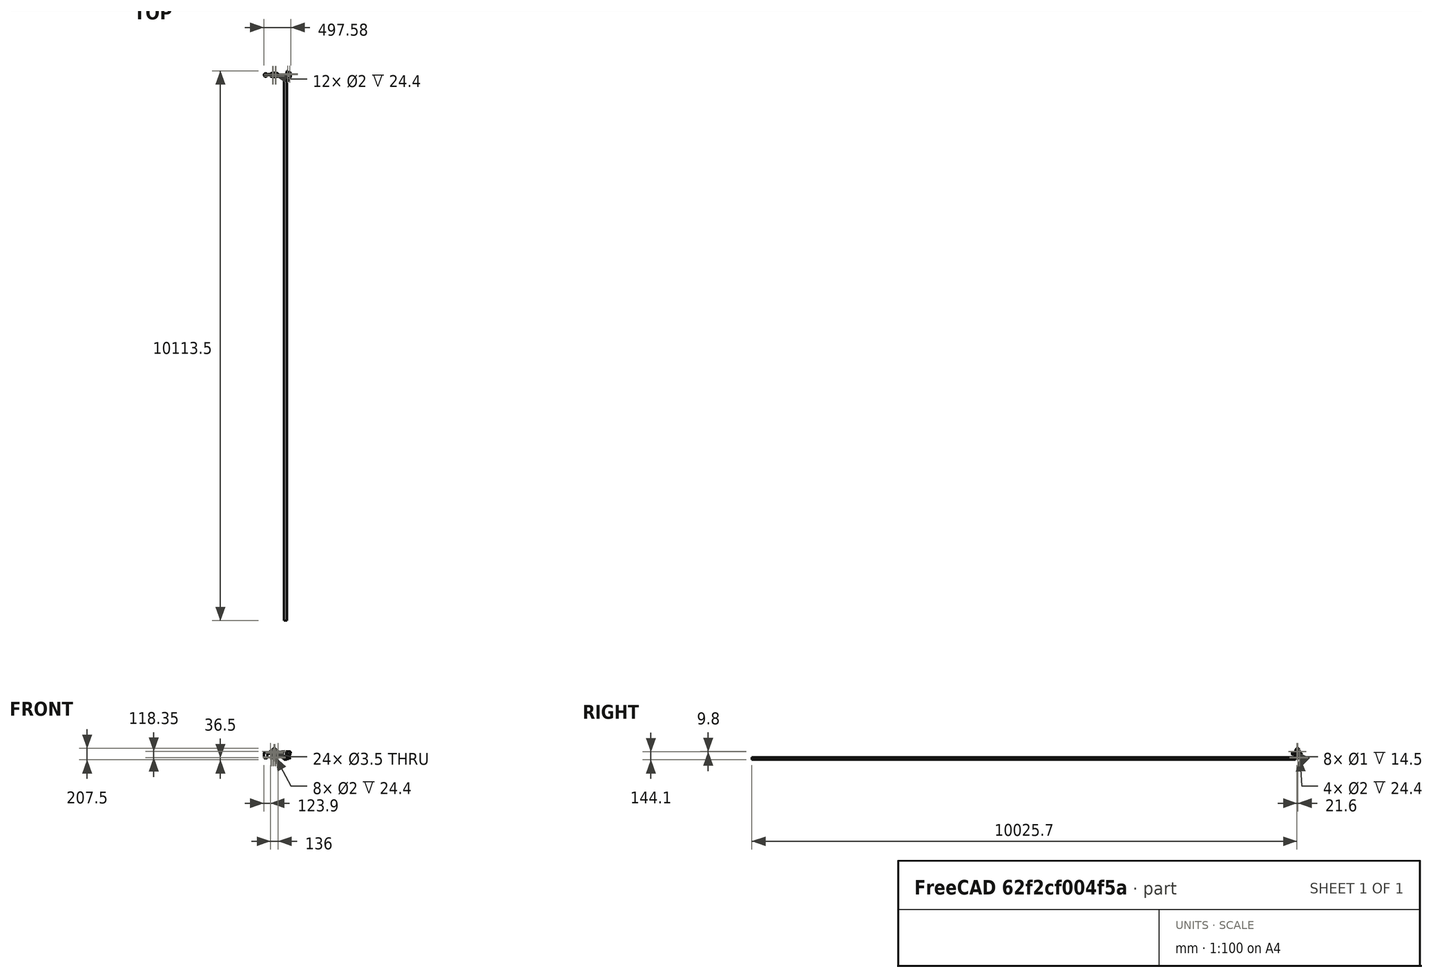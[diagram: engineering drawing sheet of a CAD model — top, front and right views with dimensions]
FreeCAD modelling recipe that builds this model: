
FCSTD DOCUMENT  (FreeCAD 0.16R6710 (Git))
Label: head_zowi_makerbot
License: CC-BY 3.0
LicenseURL: http://creativecommons.org/licenses/by/3.0/
objects: Part::Feature×140, Part::Cut×55, Part::Cylinder×55, Part::Box×45, Part::MultiFuse×37, Sketcher::SketchObject×19, Part::FeaturePython×17, App::DocumentObjectGroup×10, PartDesign::Pocket×10, Part::Mirroring×9, Part::Fillet×9, PartDesign::Pad×9, Part::Chamfer×6, Part::Prism×3, PartDesign::Fillet×2, Part::MultiCommon×2, Mesh::Feature×1
note: 437 computed .brp shape members not serialized (recipe doc carries the construction recipe); baked Part::Feature solids carry a one-line shape summary decoded from their .brp

FEATURE [Part::Feature] Part__Feature013  label="Servo-D1"
  Placement = pos=(26.5,9.5,100.6) rot=(0,1,0;3.14159rad)
  shape: bbox 55.5 x 20 x 41.74 mm, 365 faces (baked)
FEATURE [Part::Feature] Part__Feature014  label="Servo-D2"
  Placement = pos=(0,0,13) rot=(0.57735,0.57735,0.57735;2.0944rad)
  shape: bbox 41.74 x 55.5 x 20 mm, 365 faces (baked)
FEATURE [Part::Feature] Part__Feature008  label="J1"
  Placement = pos=(-10.8,44.37,77.54) rot=(0.707107,0.707107,0;3.14159rad)
  shape: bbox 11.7 x 15.49 x 2.5 mm, 224 faces (baked)
FEATURE [Part::Feature] Part__Feature009  label="J2"
  Placement = pos=(-10.8,62.15,77.54) rot=(0.707107,0.707107,0;3.14159rad)
  shape: bbox 11.7 x 15.49 x 2.5 mm, 224 faces (baked)
FEATURE [Part::Feature] Part__Feature007  label="J4"
  Placement = pos=(-10.8,59.6199,125.78) rot=(0,0,-1;1.5708rad)
  shape: bbox 11.65 x 20.57 x 2.5 mm, 290 faces (baked)
FEATURE [Part::Feature] Part__Feature010  label="J16"
  Placement = pos=(-9.55,7.19908,100.417) rot=(0.57735,0.57735,-0.57735;2.0944rad)
  shape: bbox 2.94 x 5.43 x 7.98 mm, 414 faces, 0 solids (baked)
FEATURE [Part::Feature] Part__Feature005  label="PCB"
  Placement = pos=(-12.3914,5,75) rot=(0.57735,0.57735,0.57735;2.0944rad)
  shape: bbox 1.591 x 68.6 x 53.36 mm, 426 faces (baked)
FEATURE [Part::Feature] Part__Feature004  label="J010"
  Placement = pos=(-10.8,14.8841,83.3059) rot=(0.707107,0.707107,0;3.14159rad)
  shape: bbox 10.92 x 14.61 x 8.89 mm, 41 faces (baked)
FEATURE [Part::Feature] Part__Feature011  label="U1"
  Placement = pos=(-9.2,12.159,115.511) rot=(0.57735,-0.57735,-0.57735;2.0944rad)
  shape: bbox 2.435 x 26.9 x 13 mm, 503 faces (baked)
FEATURE [Part::Feature] Part__Feature006  label="J8"
  Placement = pos=(-10.8,37.7759,125.78) rot=(0,0,-1;1.5708rad)
  shape: bbox 11.65 x 20.57 x 2.5 mm, 290 faces (baked)
FEATURE [App::DocumentObjectGroup] Group001  label="placa"
  Group = -> [Part__Feature008,Part__Feature009,Part__Feature007,Part__Feature010,Part__Feature005,Part__Feature004,Part__Feature011,Part__Feature006]
FEATURE [Part::Box] Box  label="Cube"
  Height = 24
  Length = 72
  Placement = pos=(-15,-29,-3) rot=(0,0,1;0rad)
  Width = 58
FEATURE [Part::Box] Box001  label="Cube001"
  Height = 25
  Length = 47
  Placement = pos=(-1,-21,2) rot=(0,0,1;0rad)
  Width = 42
FEATURE [Part::Box] Box002  label="Cube002"
  Height = 38
  Length = 28
  Placement = pos=(37,-45,1) rot=(0,0,1;0rad)
  Width = 88
FEATURE [Part::Box] Box003  label="Cube003"
  Height = 38
  Length = 28
  Placement = pos=(-33,-45,1) rot=(0,0,1;0rad)
  Width = 88
FEATURE [Part::Cut] Cut
  Base = -> Box
  Tool = -> Box001
FEATURE [Part::Cut] Cut001
  Base = -> Cut
  Tool = -> Box002
FEATURE [Part::Cut] Cut002
  Base = -> Cut001
  Tool = -> Box003
FEATURE [Part::Box] Box004  label="Cube004"
  Height = 60
  Length = 44
  Placement = pos=(-5,-24,-5) rot=(0,0,1;0rad)
  Width = 61
FEATURE [Part::Mirroring] Part__Mirroring  label="Servo-D1 (Mirror #1)"
  Base = (0,0,0)
  Normal = (0,1,0)
  Placement = pos=(0,72,0) rot=(0,0,1;0rad)
  Source = -> Part__Feature013
FEATURE [Part::Mirroring] Part__Mirroring001  label="Servo-D2 (Mirror #2)"
  Base = (0,0,0)
  Normal = (0,1,0)
  Placement = pos=(0,72,0) rot=(0,0,1;0rad)
  Source = -> Part__Feature014
FEATURE [Part::Cylinder] Cylinder003  label="Joint-D005"
  Angle = 360
  Height = 74.5
  Placement = pos=(-22,9.5,12) rot=(0,1,0;1.5708rad)
  Radius = 1.75
FEATURE [Part::Fillet] Fillet
  Base = -> Cut002
  Edges = 4 edges r=10: [Edge1,Edge3,Edge5,Edge14]
FEATURE [Part::Cylinder] Cylinder002  label="Joint-D004"
  Angle = 360
  Height = 53
  Placement = pos=(-9,9.5,12) rot=(0,1,0;1.5708rad)
  Radius = 10.5
FEATURE [Part::MultiFuse] Fusion
  Shapes = -> [Cylinder002]
FEATURE [Part::Cylinder] Cylinder004  label="Joint-D006"
  Angle = 360
  Height = 74.5
  Placement = pos=(16,9.5,12) rot=(0,1,0;1.5708rad)
  Radius = 5.5
FEATURE [Part::Cut] Cut003
  Base = -> Fusion
  Tool = -> Box004
FEATURE [Part::Cylinder] Cylinder005  label="Joint-D007"
  Angle = 360
  Height = 74.5
  Placement = pos=(-51,9.5,12) rot=(0,1,0;1.5708rad)
  Radius = 1.75
FEATURE [Part::Cut] Cut004
  Base = -> Cut003
  Tool = -> Cylinder004
FEATURE [Part::Cut] Cut005
  Base = -> Cut004
  Tool = -> Cylinder005
FEATURE [Part::Cylinder] Cylinder006  label="Joint-D008"
  Angle = 360
  Height = 74.5
  Placement = pos=(41.8,9.5,12) rot=(0,1,0;1.5708rad)
  Radius = 11
FEATURE [Part::Cut] Cut006
  Base = -> Cut005
  Tool = -> Cylinder006
FEATURE [Part::Cylinder] Cylinder007  label="Joint-D009"
  Angle = 360
  Height = 23.5
  Placement = pos=(16.8,9.5,58.3) rot=(0,1,0;3.14159rad)
  Radius = 11
FEATURE [Part::Cylinder] Cylinder008  label="Joint-D010"
  Angle = 360
  Height = 21.5
  Placement = pos=(16,-24.5,7) rot=(0,1,0;1.5708rad)
  Radius = 1.75
FEATURE [Part::Cylinder] Cylinder009  label="Joint-D011"
  Angle = 360
  Height = 21.5
  Placement = pos=(32,-24.5,7) rot=(0,1,0;1.5708rad)
  Radius = 3
FEATURE [Part::MultiFuse] Fusion001
  Shapes = -> [Cylinder009,Cylinder008]
FEATURE [Part::MultiFuse] Fusion002
  Placement = pos=(0,0,10) rot=(0,0,1;0rad)
  Shapes = -> [Cylinder009,Cylinder008]
FEATURE [Part::MultiFuse] Fusion003
  Placement = pos=(0,49,0) rot=(0,0,1;0rad)
  Shapes = -> [Cylinder009,Cylinder008]
FEATURE [Part::MultiFuse] Fusion004
  Placement = pos=(0,49,10) rot=(0,0,1;0rad)
  Shapes = -> [Cylinder009,Cylinder008]
FEATURE [Part::Box] Box006  label="Cube006"
  Height = 21
  Length = 4
  Placement = pos=(25.5,-28,2) rot=(0,0,1;0rad)
  Width = 56
FEATURE [Part::Cylinder] Cylinder010  label="Joint-D012"
  Angle = 360
  Height = 74.5
  Placement = pos=(17,9.5,12) rot=(0,0,1;0rad)
  Radius = 5.5
FEATURE [Part::Box] Box007  label="Cube007"
  Height = 6
  Length = 3
  Placement = pos=(18.5,-28,4) rot=(0,0,1;0rad)
  Width = 56
FEATURE [Part::Box] Box008  label="Cube008"
  Height = 6
  Length = 3
  Placement = pos=(18.5,-28,14) rot=(0,0,1;0rad)
  Width = 56
FEATURE [Part::Cylinder] Cylinder011  label="Joint-D013"
  Angle = 360
  Height = 74.5
  Placement = pos=(-3,9.5,12) rot=(0,1,0;1.5708rad)
  Radius = 2.75
FEATURE [Part::Box] Box009  label="Cube009"
  Height = 5
  Length = 80
  Placement = pos=(-23,-4,63) rot=(0,0,1;0rad)
  Width = 80
FEATURE [Part::Box] Box010  label="Cube010"
  Height = 9
  Length = 7
  Placement = pos=(-1,-1,63) rot=(0,0,1;0rad)
  Width = 74
FEATURE [Part::Box] Box011  label="Cube011"
  Height = 9
  Length = 7
  Placement = pos=(47,-1,63) rot=(0,0,1;0rad)
  Width = 74
FEATURE [Part::MultiFuse] Fusion005
  Placement = pos=(44,39,98) rot=(0,1,0;1.5708rad)
  Shapes = -> [Cylinder009,Cylinder008]
FEATURE [Part::MultiFuse] Fusion008
  Placement = pos=(44,29,98) rot=(0,1,0;1.5708rad)
  Shapes = -> [Cylinder009,Cylinder008]
FEATURE [Part::MultiFuse] Fusion009
  Placement = pos=(-5,39,98) rot=(0,1,0;1.5708rad)
  Shapes = -> [Cylinder009,Cylinder008]
FEATURE [Part::MultiFuse] Fusion010
  Placement = pos=(-5,29,98) rot=(0,1,0;1.5708rad)
  Shapes = -> [Cylinder009,Cylinder008]
FEATURE [Part::Box] Box012  label="Cube012"
  Height = 9
  Length = 70
  Placement = pos=(-6,8.5,70) rot=(0,0,1;0rad)
  Width = 2
FEATURE [Part::MultiFuse] Fusion011
  Shapes = -> [Box012,Fusion009,Fusion010,Fusion008,Fusion005]
FEATURE [Part::MultiFuse] Fusion012
  Placement = pos=(0,53,0) rot=(0,0,1;0rad)
  Shapes = -> [Box012,Fusion009,Fusion010,Fusion008,Fusion005]
FEATURE [Part::MultiFuse] Fusion013
  Shapes = -> [Box009,Box011,Box010]
FEATURE [Part::Cut] Cut018
  Base = -> Fusion013
  Tool = -> Fusion012
FEATURE [Part::Cut] Cut019
  Base = -> Cut018
  Tool = -> Fusion011
FEATURE [Part::Box] Box014  label="Cube014"
  Height = 43
  Length = 41
  Placement = pos=(6,-1,59) rot=(0,0,1;0rad)
  Width = 21
FEATURE [Part::Box] Box015  label="Cube015"
  Height = 43
  Length = 41
  Placement = pos=(6,52,59) rot=(0,0,1;0rad)
  Width = 21
FEATURE [Part::Cut] Cut020
  Base = -> Cut019
  Tool = -> Box014
FEATURE [Part::Cut] Cut021
  Base = -> Cut020
  Tool = -> Box015
FEATURE [Part::Box] Box016  label="Cube016"
  Height = 12
  Length = 6
  Placement = pos=(-11.5,3,69) rot=(0,0,1;0rad)
  Width = 3
FEATURE [Part::Box] Box017  label="Cube017"
  Height = 12
  Length = 16
  Placement = pos=(-20,-1,63) rot=(0,0,1;0rad)
  Width = 74
FEATURE [Part::Box] Box018  label="Cube018"
  Height = 12
  Length = 6
  Placement = pos=(-11.5,66,69) rot=(0,0,1;0rad)
  Width = 3
FEATURE [Part::MultiFuse] Fusion014
  Shapes = -> [Cut021,Box017]
FEATURE [Part::Cut] Cut022
  Base = -> Fusion014
  Tool = -> Box016
FEATURE [Part::Cut] Cut023
  Base = -> Cut022
  Tool = -> Box018
FEATURE [PartDesign::Fillet] Fillet011  label="horn"
  Placement = pos=(38.5,9.5,13) rot=(0,0,-1;1.5708rad)
  Radius = 0.5
FEATURE [Part::Cylinder] Cylinder021  label="Joint-D014"
  Angle = 360
  Height = 52.5
  Placement = pos=(19,9.5,20.35) rot=(0,1,0;1.5708rad)
  Radius = 1
FEATURE [Part::Cylinder] Cylinder022  label="Joint-D015"
  Angle = 360
  Height = 52.5
  Placement = pos=(19,2,9.5) rot=(0,1,0;1.5708rad)
  Radius = 1
FEATURE [Part::Cylinder] Cylinder023  label="Joint-D016"
  Angle = 360
  Height = 52.5
  Placement = pos=(19,17,9.5) rot=(0,1,0;1.5708rad)
  Radius = 1
FEATURE [Part::MultiFuse] Fusion017
  Placement = pos=(0,0,-1) rot=(0,0,1;0rad)
  Shapes = -> [Cylinder022,Cylinder021,Cylinder023]
FEATURE [Part::MultiFuse] Fusion018
  Placement = pos=(4,0,101) rot=(0,1,0;1.5708rad)
  Shapes = -> [Cylinder022,Cylinder021,Cylinder023]
FEATURE [PartDesign::Fillet] Fillet012  label="horn001"
  Placement = pos=(16.8,9.5,62.5) rot=(-0.57735,0.57735,-0.57735;2.0944rad)
  Radius = 0.5
FEATURE [Part::Mirroring] Part__Mirroring003  label="horn (Mirror #4)"
  Base = (41.6,1.90735e-06,13)
  Normal = (0,1,-1.19209e-07)
  Placement = pos=(0,72,0) rot=(0,0,1;0rad)
  Source = -> Fillet011
FEATURE [Part::Mirroring] Part__Mirroring004  label="horn001 (Mirror #5)"
  Base = (16.8,7.62939e-06,59.3998)
  Normal = (0,1,-1.19209e-07)
  Placement = pos=(0,72,0) rot=(0,0,1;0rad)
  Source = -> Fillet012
FEATURE [Part::Chamfer] Chamfer
  Base = -> Fillet
  Edges = 3 edges r=3: [Edge18,Edge33,Edge37]
FEATURE [Part::Cut] Cut008
  Base = -> Chamfer
  Tool = -> Cylinder003
FEATURE [Part::Cut] Cut010
  Base = -> Cut008
  Tool = -> Box006
FEATURE [Part::Cut] Cut011
  Base = -> Cut010
  Tool = -> Box008
FEATURE [Part::Cut] Cut012
  Base = -> Cut011
  Tool = -> Box007
FEATURE [Part::Cut] Cut013
  Base = -> Cut012
  Tool = -> Fusion004
FEATURE [Part::Cut] Cut014
  Base = -> Cut013
  Tool = -> Fusion003
FEATURE [Part::Cut] Cut015
  Base = -> Cut014
  Tool = -> Fusion002
FEATURE [Part::Cut] Cut016
  Base = -> Cut015
  Tool = -> Fusion001
FEATURE [Part::Cut] Cut017  label="pie"
  Base = -> Cut016
  Tool = -> Cylinder011
FEATURE [Part::Box] Box024  label="Cube024"
  Height = 23
  Length = 6
  Placement = pos=(0,19,7) rot=(0,0,1;0rad)
  Width = 36
FEATURE [Part::Cut] Cut039  label="pie-D"
  Base = -> Cut017
  Placement = pos=(0,0,1) rot=(0,0,1;0rad)
  Tool = -> Box024
FEATURE [Part::Mirroring] Part__Mirroring006  label="pie-I"
  Base = (0,0,0)
  Normal = (0,1,0)
  Placement = pos=(0,72,0) rot=(0,0,1;0rad)
  Source = -> Cut039
FEATURE [Part::Cut] Cut044
  Base = -> Cut006
  Tool = -> Box004
FEATURE [Part::Cut] Cut045
  Base = -> Cut044
  Tool = -> Cylinder007
FEATURE [Part::Cut] Cut046
  Base = -> Cut045
  Tool = -> Fusion018
FEATURE [Part::Cut] Cut047
  Base = -> Cut046
  Tool = -> Fusion017
FEATURE [Part::Cut] Cut048
  Base = -> Cut047
  Placement = pos=(0,0,1) rot=(0,0,1;0rad)
  Tool = -> Cylinder010
FEATURE [Part::Chamfer] Chamfer001
  Base = -> Cut048
  Edges = 1 edges r=4: [Edge61]
FEATURE [Part::Chamfer] Chamfer002  label="pata-D"
  Base = -> Chamfer001
  Edges = 1 edges r=8: [Edge58]
FEATURE [Part::Mirroring] Part__Mirroring007  label="pata-I"
  Base = (17.5,3.8147e-06,32.25)
  Normal = (0,1,-1.19209e-07)
  Placement = pos=(0,72,0) rot=(0,0,1;0rad)
  Source = -> Chamfer002
FEATURE [Part::Cylinder] Cylinder012  label="Cylinder030"
  Angle = 360
  Height = 31
  Placement = pos=(-8.5,92,71.5) rot=(1,0,0;1.5708rad)
  Radius = 1.75
FEATURE [Part::Cut] Cut024
  Base = -> Cut023
  Tool = -> Cylinder012
FEATURE [Part::Cylinder] Cylinder013  label="Cylinder001"
  Angle = 360
  Height = 31
  Placement = pos=(-8.5,11,71.5) rot=(1,0,0;1.5708rad)
  Radius = 1.75
FEATURE [Part::Feature] Part__Feature  label="Portapilas008"
  shape: bbox 2e-07 x 47.97 x 51.59 mm, 1 faces, 0 solids (baked)
FEATURE [Part::Feature] Part__Feature015  label="Portapilas007"
  shape: bbox 9.213 x 1.1 x 48.01 mm, 3 faces, 0 solids (baked)
FEATURE [Part::Feature] Part__Feature016  label="Portapilas006"
  shape: bbox 9.213 x 1.1 x 48.01 mm, 3 faces, 0 solids (baked)
FEATURE [Part::Feature] Part__Feature017  label="Portapilas005"
  shape: bbox 9.213 x 1.1 x 48.01 mm, 3 faces, 0 solids (baked)
FEATURE [Part::Feature] Part__Feature018  label="Portapilas004"
  shape: bbox 9.213 x 1.1 x 48.01 mm, 3 faces, 0 solids (baked)
FEATURE [Part::Feature] Part__Feature019  label="Portapilas003"
  shape: bbox 9.213 x 1.1 x 48.01 mm, 3 faces, 0 solids (baked)
FEATURE [Part::Feature] Part__Feature020  label="Portapilas002"
  shape: bbox 9.213 x 1.1 x 48.01 mm, 3 faces, 0 solids (baked)
FEATURE [Part::Feature] Part__Feature021  label="Portapilas001"
  shape: bbox 16.42 x 48.04 x 51.59 mm, 26 faces, 0 solids (baked)
FEATURE [Part::Feature] Part__Feature022  label="Portapilas"
  shape: bbox 21.03 x 69.14 x 72.63 mm, 394 faces, 0 solids (baked)
FEATURE [Part::MultiFuse] Fusion019  label="peterpilas"
  Placement = pos=(23,77.5,76) rot=(0,0,1;1.5708rad)
  Shapes = -> [Part__Feature022,Part__Feature021,Part__Feature020,Part__Feature019,Part__Feature018,Part__Feature017,Part__Feature016,Part__Feature015,Part__Feature]
FEATURE [Part::Feature] Part__Feature023  label="Ultrasonido_BAT"
  Placement = pos=(-17,36,59.5) rot=(0,0,1;0rad)
  shape: bbox 18.72 x 56 x 27.52 mm, 81 faces (baked)
FEATURE [Part::Cut] Cut050
  Base = -> Cut024
  Tool = -> Cylinder013
FEATURE [Part::Box] Box032  label="Cube032"
  Height = 20
  Length = 3
  Placement = pos=(51,20,66) rot=(0,0,1;0rad)
  Width = 32
FEATURE [Part::Box] Box033  label="Cube033"
  Height = 54
  Length = 4.5
  Placement = pos=(-20,6,64) rot=(0,0,1;0rad)
  Width = 60
FEATURE [Part::Box] Box035  label="Cube035"
  Height = 68
  Length = 6
  Placement = pos=(-23.5,17,68) rot=(0,0,1;0rad)
  Width = 38
FEATURE [Part::Box] Box036  label="Cube034"
  Height = 17
  Length = 13
  Placement = pos=(-14,20,62) rot=(0,0,1;0rad)
  Width = 32
FEATURE [Part::Fillet] Fillet018002
  Base = -> Box036
  Edges = 4 edges r=5: [Edge1,Edge3,Edge5,Edge7]
FEATURE [Part::Cylinder] Cylinder  label="Cylinder093"
  Angle = 360
  Height = 31
  Placement = pos=(-49.5,29,111.5) rot=(0,1,0;1.5708rad)
  Radius = 1.75
FEATURE [Part::Cylinder] Cylinder040  label="Cylinder094"
  Angle = 360
  Height = 31
  Placement = pos=(-49.5,49,91.5) rot=(0,1,0;1.5708rad)
  Radius = 1.75
FEATURE [Part::Cylinder] Cylinder041  label="Cylinder095"
  Angle = 360
  Height = 31
  Placement = pos=(-49.5,49,111.5) rot=(0,1,0;1.5708rad)
  Radius = 1.75
FEATURE [Part::MultiFuse] Fusion025
  Shapes = -> [Box032,Cut050]
FEATURE [Part::Box] Box037  label="Cube036"
  Height = 44
  Length = 61
  Placement = pos=(-9,22,66) rot=(0,0,1;0rad)
  Width = 28
FEATURE [Part::MultiFuse] Fusion026
  Shapes = -> [Fusion025,Box033]
FEATURE [Part::Cut] Cut051
  Base = -> Fusion026
  Tool = -> Fillet018002
FEATURE [Part::Box] Box038  label="Cube037"
  Height = 11
  Length = 8
  Placement = pos=(-11.5,-52,95) rot=(0,0,1;0rad)
  Width = 58
FEATURE [Part::Cylinder] Cylinder042  label="Cylinder096"
  Angle = 360
  Height = 61
  Placement = pos=(-5,124,89.6) rot=(1,0,0;1.5708rad)
  Radius = 4
FEATURE [Part::Cylinder] Cylinder043  label="Cylinder097"
  Angle = 360
  Height = 63
  Placement = pos=(-3,11,83.5) rot=(1,0,0;1.5708rad)
  Radius = 6
FEATURE [Part::Box] Box039  label="Cube038"
  Height = 66
  Length = 76
  Placement = pos=(-21,-2,63) rot=(0,0,1;0rad)
  Width = 76
FEATURE [Part::Cylinder] Cylinder044  label="Cylinder098"
  Angle = 360
  Height = 23
  Placement = pos=(-8.5,1,71.5) rot=(1,0,0;1.5708rad)
  Radius = 1.75
FEATURE [Part::Cylinder] Cylinder045  label="Cylinder099"
  Angle = 360
  Height = 31
  Placement = pos=(-8.5,94,71.5) rot=(1,0,0;1.5708rad)
  Radius = 1.75
FEATURE [Part::Fillet] Fillet018007
  Base = -> Box039
  Edges = 8 edges r=3: [Edge1,Edge2,Edge3,Edge5,Edge6,Edge7,Edge10,Edge12]
FEATURE [Part::Box] Box040  label="Cube039"
  Height = 6
  Length = 81
  Placement = pos=(-23.5,-4.5,63) rot=(0,0,1;0rad)
  Width = 81
FEATURE [Part::Fillet] Fillet018008
  Base = -> Box040
  Edges = 4 edges r=5: [Edge1,Edge3,Edge5,Edge7]
  Placement = pos=(0,0,-1) rot=(0,0,1;0rad)
FEATURE [Part::Cylinder] Cylinder046  label="Cylinder100"
  Angle = 360
  Height = 45
  Placement = pos=(-8.5,-7,71.5) rot=(1,0,0;1.5708rad)
  Radius = 4
FEATURE [Part::Cylinder] Cylinder047  label="Cylinder101"
  Angle = 360
  Height = 45
  Placement = pos=(-8.5,124,71.5) rot=(1,0,0;1.5708rad)
  Radius = 4
FEATURE [Part::MultiFuse] Fusion033
  Shapes = -> [Fillet018007,Fillet018008]
FEATURE [Part::MultiFuse] Fusion034  label="corte-positivo"
  Shapes = -> [Fusion033,Cylinder042,Cylinder047,Cylinder045,Cylinder046,Cylinder043,Box038,Cylinder044]
FEATURE [Part::Cylinder] Cylinder053  label="Cylinder102"
  Angle = 360
  Height = 31
  Placement = pos=(-49.5,29,91.5) rot=(0,1,0;1.5708rad)
  Radius = 1.75
FEATURE [Part::MultiFuse] Fusion038
  Placement = pos=(14,0,0) rot=(0,0,1;0rad)
  Shapes = -> [Cylinder053,Cylinder040,Cylinder041,Cylinder]
FEATURE [App::DocumentObjectGroup] Group004  label="electronic"
  Group = -> [Part__Mirroring,Part__Mirroring001,Part__Mirroring003,Part__Mirroring004,Fusion019,Part__Feature023,Group001]
FEATURE [App::DocumentObjectGroup] Group005  label="aux"
  Group = -> [Fusion034]
FEATURE [Part::Cut] Cut066
  Base = -> Cut051
  Tool = -> Box037
FEATURE [Part::Chamfer] Chamfer003
  Base = -> Cut066
  Edges = 1 edges r=3: [Edge86]
FEATURE [Sketcher::SketchObject] Sketch
  Placement = pos=(-22,0,0) rot=(0.57735,-0.57735,-0.57735;2.0944rad)
  sketch-geometry (4):
    g0: ArcOfCircle CenterX=-49 CenterY=111.5 CenterZ=0 NormalX=0 NormalY=0 NormalZ=1 Radius=3.5 StartAngle=9.1497e-08 EndAngle=3.14159
    g1: LineSegment StartX=-52.5 StartY=111.5 StartZ=0 EndX=-52.5 EndY=91.5 EndZ=0
    g2: LineSegment StartX=-45.5 StartY=111.5 StartZ=0 EndX=-45.5 EndY=91.5 EndZ=0
    g3: ArcOfCircle CenterX=-49 CenterY=91.5 CenterZ=0 NormalX=0 NormalY=0 NormalZ=1 Radius=3.5 StartAngle=3.14159 EndAngle=6.28319
  constraints (13):
    c: DistanceX(g-1,g0) = -49
    c: DistanceY(g-1,g0) = 111.5
    c: Radius(g0) = 3.5
    c: Vertical(g1)
    c: Vertical(g2)
    c: Coincident(g1,g0)
    c: Coincident(g2,g0)
    c: Tangent(g2,g0)
    c: Tangent(g1,g0)
    c: Coincident(g3,g1)
    c: Coincident(g3,g2)
    c: Equal(g3,g0)
    c: Distance(g3,g0) = 20
FEATURE [PartDesign::Pad] Pad
  Length = 5
  Length2 = 100
  Placement = pos=(-22,0,0) rot=(0.57735,-0.57735,-0.57735;2.0944rad)
  Reversed = true
  Sketch = -> Sketch
  Type = 0
FEATURE [Part::FeaturePython] Clone  label="Clone of Pad"  # Draft clone (typed FeaturePython)
  Objects = -> [Pad]
  Placement = pos=(-22,-20,0) rot=(0.57735,-0.57735,-0.57735;2.0944rad)
  Scale = (1,1,1)
FEATURE [Part::MultiFuse] Fusion039
  Placement = pos=(4.5,0,0) rot=(0,0,1;0rad)
  Shapes = -> [Pad,Clone]
FEATURE [Part::MultiFuse] Fusion040
  Shapes = -> [Chamfer003,Fusion039]
FEATURE [Part::Cut] Cut067
  Base = -> Fusion040
  Tool = -> Fusion038
FEATURE [Part::Cut] Cut068
  Base = -> Cut067
  Tool = -> Box035
FEATURE [Sketcher::SketchObject] Sketch001  label="leg-sketch-1"
  Placement = pos=(0,0,0) rot=(0.57735,0.57735,0.57735;2.0944rad)
  sketch-geometry (5):
    g0: LineSegment StartX=-49 StartY=10.5 StartZ=0 EndX=0 EndY=10.5 EndZ=0
    g1: LineSegment StartX=0 StartY=10.5 StartZ=0 EndX=0 EndY=-10.5 EndZ=0
    g2: LineSegment StartX=0 StartY=-10.5 StartZ=0 EndX=-49 EndY=-10.5 EndZ=0
    g3: LineSegment [constr] StartX=-49 StartY=-10.5 StartZ=0 EndX=-49 EndY=10.5 EndZ=0
    g4: ArcOfCircle CenterX=-49 CenterY=0 CenterZ=0 NormalX=0 NormalY=0 NormalZ=1 Radius=10.5 StartAngle=1.5708 EndAngle=4.71239
  constraints (15):
    c: Coincident(g0,g1)
    c: Coincident(g1,g2)
    c: Coincident(g2,g3)
    c: Coincident(g3,g0)
    c: Horizontal(g0)
    c: Horizontal(g2)
    c: Vertical(g1)
    c: Vertical(g3)
    c: PointOnObject(g4,g3)
    c: Coincident(g4,g0)
    c: Coincident(g4,g2)
    c: PointOnObject(g4,g-1)
    c: PointOnObject(g0,g-2)
    c: DistanceX(g0) = 49
    c: DistanceY(g1) = -21
FEATURE [PartDesign::Pad] Pad001  label="leg-block-1"
  Length = 53
  Length2 = 100
  Midplane = true
  Placement = pos=(0,0,0) rot=(0.57735,0.57735,0.57735;2.0944rad)
  Sketch = -> Sketch001
  Type = 0
FEATURE [Sketcher::SketchObject] Sketch002  label="leg-top-sketch"
  ExternalGeometry = -> [Pad001]
  Placement = pos=(0,0,10.5) rot=(0,0,-1;1.5708rad)
  Support = -> Pad001 [Face1]
  sketch-geometry (9):
    g0: LineSegment StartX=64 StartY=21.5 StartZ=0 EndX=10 EndY=21.5 EndZ=0
    g1: LineSegment StartX=6 StartY=17.5 StartZ=0 EndX=6 EndY=-19.5 EndZ=0
    g2: LineSegment StartX=9 StartY=-22.5 StartZ=0 EndX=64 EndY=-22.5 EndZ=0
    g3: LineSegment StartX=64 StartY=-22.5 StartZ=0 EndX=64 EndY=21.5 EndZ=0
    g4: LineSegment StartX=6 StartY=17.5 StartZ=0 EndX=10 EndY=21.5 EndZ=0
    g5: LineSegment [constr] StartX=6 StartY=17.5 StartZ=0 EndX=6 EndY=21.5 EndZ=0
    g6: LineSegment StartX=6 StartY=-19.5 StartZ=0 EndX=9 EndY=-22.5 EndZ=0
    g7: LineSegment [constr] StartX=9 StartY=-22.5 StartZ=0 EndX=6 EndY=-22.5 EndZ=0
    g8: LineSegment [constr] StartX=6 StartY=-22.5 StartZ=0 EndX=6 EndY=-19.5 EndZ=0
  constraints (26):
    c: Coincident(g2,g3)
    c: Coincident(g3,g0)
    c: Horizontal(g0)
    c: Horizontal(g2)
    c: Vertical(g1)
    c: Vertical(g3)
    c: DistanceY(g-3,g5) = -5
    c: DistanceY(g7,g-4) = -4
    c: Angle(g-2,g4) = 2.35619
    c: Coincident(g1,g4)
    c: Coincident(g5,g1)
    c: Vertical(g5)
    c: DistanceY(g1,g7) = -40
    c: DistanceX(g5,g-3) = -6
    c: Coincident(g0,g4)
    c: PointOnObject(g5,g0)
    c: DistanceX(g-3,g0) = 15
    c: Coincident(g2,g6)
    c: Coincident(g7,g2)
    c: Horizontal(g7)
    c: DistanceX(g7) = -3
    c: Coincident(g1,g6)
    c: Coincident(g8,g7)
    c: Coincident(g8,g1)
    c: Equal(g8,g7)
    c: Vertical(g8)
FEATURE [PartDesign::Pocket] Pocket  label="leg-block-2"
  Length = 5
  Placement = pos=(0,0,0) rot=(0.57735,0.57735,0.57735;2.0944rad)
  Sketch = -> Sketch002
  Type = 1
FEATURE [Sketcher::SketchObject] Sketch003  label="ankle-rounded-horn-sketch"
  ExternalGeometry = -> [Pocket]
  Placement = pos=(26.5,0,0) rot=(0.57735,0.57735,0.57735;2.0944rad)
  Support = -> Pocket [Face4]
  sketch-geometry (1):
    g0: Circle CenterX=-49 CenterY=0 CenterZ=0 NormalX=0 NormalY=0 NormalZ=1 Radius=10.75
  constraints (2):
    c: Coincident(g0,g-3)
    c: Radius(g0) = 10.75
FEATURE [PartDesign::Pocket] Pocket001  label="ankle-rounded-horn-cutout"
  Length = 2.2
  Placement = pos=(0,0,0) rot=(0.57735,0.57735,0.57735;2.0944rad)
  Sketch = -> Sketch003
  Type = 0
FEATURE [Sketcher::SketchObject] Sketch004  label="ankle-rear-shaft-drill-sketch"
  ExternalGeometry = -> [Pocket001]
  Placement = pos=(-26.5,0,0) rot=(0.57735,0.57735,-0.57735;4.18879rad)
  Support = -> Pocket001 [Face2]
  sketch-geometry (1):
    g0: Circle CenterX=-49 CenterY=0 CenterZ=0 NormalX=0 NormalY=0 NormalZ=1 Radius=1.75
  constraints (2):
    c: Coincident(g0,g-3)
    c: Radius(g0) = 1.75
FEATURE [PartDesign::Pocket] Pocket002  label="ankle-rear-shaft-drill"
  Length = 0
  Placement = pos=(0,0,0) rot=(0.57735,0.57735,0.57735;2.0944rad)
  Sketch = -> Sketch004
  Type = 2
FEATURE [Sketcher::SketchObject] Sketch005  label="hip-rounded-horn-cutout-sketch"
  Placement = pos=(0,-6,0) rot=(-0.57735,-0.57735,0.57735;4.18879rad)
  Support = -> Pocket002 [Face10]
  sketch-geometry (1):
    g0: Circle CenterX=0 CenterY=0 CenterZ=0 NormalX=0 NormalY=0 NormalZ=1 Radius=11
  constraints (2):
    c: Coincident(g0,g-1)
    c: Radius(g0) = 11
FEATURE [PartDesign::Pocket] Pocket003  label="hip-rounded-horn-cutout"
  Length = 3.3
  Placement = pos=(0,0,0) rot=(0.57735,0.57735,0.57735;2.0944rad)
  Sketch = -> Sketch005
  Type = 0
FEATURE [Sketcher::SketchObject] Sketch006  label="horn-side-chamfer-sketch"
  ExternalGeometry = -> [Pocket003]
  Placement = pos=(0,0,10.5) rot=(0,0,-1;1.5708rad)
  Support = -> Pocket003 [Face1]
  sketch-geometry (3):
    g0: LineSegment StartX=0 StartY=18.5 StartZ=0 EndX=8 EndY=26.5 EndZ=0
    g1: LineSegment StartX=0 StartY=18.5 StartZ=0 EndX=0 EndY=26.5 EndZ=0
    g2: LineSegment StartX=0 StartY=26.5 StartZ=0 EndX=8 EndY=26.5 EndZ=0
  constraints (8):
    c: PointOnObject(g0,g-2)
    c: PointOnObject(g0,g-3)
    c: Angle(g-2,g0) = 2.35619
    c: DistanceY(g-3,g0) = -8
    c: Coincident(g0,g1)
    c: Coincident(g1,g-3)
    c: Coincident(g1,g2)
    c: Coincident(g2,g0)
FEATURE [PartDesign::Pocket] Pocket004  label="horn-side-chamfer"
  Length = 5
  Placement = pos=(0,0,0) rot=(0.57735,0.57735,0.57735;2.0944rad)
  Sketch = -> Sketch006
  Type = 1
FEATURE [Part::Cylinder] Cylinder054  label="servo-shaft-drill"
  Angle = 360
  Height = 20
  Placement = pos=(0,10,0) rot=(1,0,0;1.5708rad)
  Radius = 5.5
FEATURE [Part::Cylinder] Cylinder055  label="servo-horn-small-drill-master"
  Angle = 360
  Height = 20
  Placement = pos=(-3.5,10,7.5) rot=(1,0,0;1.5708rad)
  Radius = 1
FEATURE [Part::FeaturePython] Clone001  label="Clone of servo-horn-small-drill-master"  # Draft clone (typed FeaturePython)
  Objects = -> [Cylinder055]
  Placement = pos=(7.35,10,-2.33815e-06) rot=(1,0,0;1.5708rad)
  Scale = (1,1,1)
FEATURE [Part::FeaturePython] Clone002  label="Clone of servo-horn-small-drill-master001"  # Draft clone (typed FeaturePython)
  Objects = -> [Cylinder055]
  Placement = pos=(-3.5,10,-7.5) rot=(1,0,0;1.5708rad)
  Scale = (1,1,1)
FEATURE [Part::MultiFuse] Fusion041  label="servo-Drills-block1-master"
  Shapes = -> [Clone001,Clone002,Cylinder055,Cylinder054]
FEATURE [Part::FeaturePython] Clone003  label="Clone of servo-Drills-block1-master"  # Draft clone (typed FeaturePython)
  Objects = -> [Fusion041]
  Placement = pos=(22,-49,6.96015e-06) rot=(0,0,1;1.5708rad)
  Scale = (1,1,1)
FEATURE [Part::MultiFuse] Fusion042  label="Servo-horn-drills"
  Shapes = -> [Fusion041,Clone003]
FEATURE [Part::Cut] Cut070  label="Leg"
  Base = -> Pocket004
  Tool = -> Fusion042
FEATURE [App::DocumentObjectGroup] Group007  label="Leg-src"
  Group = -> [Pad001,Pocket,Pocket001,Pocket002,Pocket003,Cut070]
FEATURE [App::DocumentObjectGroup] Group006  label="src"
  Group = -> [Group007]
FEATURE [Part::Feature] Fusion043  label="soft-drink-can"
  Placement = pos=(-397.85,47.19,0) rot=(0,0,-1;1.5708rad)
  shape: bbox 66.1 x 66.1 x 115.2 mm, 53 faces (baked)
FEATURE [App::DocumentObjectGroup] Group018  label="development"
  Group = -> [Group006]
FEATURE [Part::Fillet] Fillet018013  label="chass"
  Base = -> Cut068
  Edges = 4 edges r=3: [Edge75,Edge118,Edge216,Edge229]
FEATURE [Sketcher::SketchObject] Sketch010
  Placement = pos=(-1,0,0) rot=(0.57735,0.57735,0.57735;2.0944rad)
  sketch-geometry (5):
    g0: LineSegment StartX=-35.7295 StartY=116.767 StartZ=0 EndX=-15.7739 EndY=107.988 EndZ=0
    g1: LineSegment StartX=-7.00034 StartY=107.988 StartZ=0 EndX=-7.00034 EndY=136.643 EndZ=0
    g2: LineSegment StartX=-7.00034 StartY=136.643 StartZ=0 EndX=-31.551 EndY=136.643 EndZ=0
    g3: ArcOfCircle CenterX=-31.551 CenterY=126.266 CenterZ=0 NormalX=0 NormalY=0 NormalZ=1 Radius=10.3774 StartAngle=1.5708 EndAngle=4.29797
    g4: LineSegment StartX=-15.7739 StartY=107.988 StartZ=0 EndX=-7.00034 EndY=107.988 EndZ=0
  constraints (10):
    c: Coincident(g1,g2)
    c: Coincident(g2,g3)
    c: Coincident(g0,g3)
    c: Horizontal(g2)
    c: Vertical(g1)
    c: Tangent(g3,g0)
    c: Tangent(g3,g2)
    c: Coincident(g1,g4)
    c: Coincident(g0,g4)
    c: Horizontal(g4)
FEATURE [PartDesign::Pad] Pad005
  Length = 42
  Length2 = 100
  Placement = pos=(-1,0,0) rot=(0.57735,0.57735,0.57735;2.0944rad)
  Sketch = -> Sketch010
  Type = 0
FEATURE [Part::MultiFuse] Fusion045  label="servo-src"
  Placement = pos=(23,4.5,120) rot=(0,0.707107,-0.707107;3.14159rad)
  Shapes = -> [Part__Feature,Part__Feature004,Part__Feature005]
FEATURE [Part::FeaturePython] Clone007  label="microservo"  # Draft clone (typed FeaturePython)
  Objects = -> [Fusion045]
  Placement = pos=(-207.5,47,122.5) rot=(0.57735,0.57735,0.57735;2.0944rad)
  Scale = (1,1,1)
FEATURE [Part::FeaturePython] Clone008  label="microservo001"  # Draft clone (typed FeaturePython)
  Objects = -> [Fusion045]
  Placement = pos=(-270.5,47,122.5) rot=(0.57735,0.57735,-0.57735;4.18879rad)
  Scale = (1,1,1)
FEATURE [Part::FeaturePython] Clone009  label="microservo002"  # Draft clone (typed FeaturePython)
  Objects = -> [Fusion045]
  Placement = pos=(-307,51.5,122.5) rot=(0.57735,-0.57735,0.57735;2.0944rad)
  Scale = (1,1,1)
FEATURE [Sketcher::SketchObject] Sketch012
  Placement = pos=(3,-12,-1) rot=(0.57735,0.57735,0.57735;2.0944rad)
  sketch-geometry (4):
    g0: LineSegment StartX=-4.88207 StartY=101.941 StartZ=0 EndX=-4.88207 EndY=138.56 EndZ=0
    g1: LineSegment StartX=-4.88207 StartY=138.56 StartZ=0 EndX=-40.5711 EndY=142.374 EndZ=0
    g2: LineSegment StartX=-40.5711 StartY=142.374 StartZ=0 EndX=-40.5711 EndY=120.688 EndZ=0
    g3: LineSegment StartX=-40.5711 StartY=120.688 StartZ=0 EndX=-4.88207 EndY=101.941 EndZ=0
  constraints (6):
    c: Coincident(g0,g1)
    c: Coincident(g1,g2)
    c: Coincident(g2,g3)
    c: Coincident(g0,g3)
    c: Vertical(g0)
    c: Vertical(g2)
FEATURE [PartDesign::Pad] Pad007
  Length = 34
  Length2 = 100
  Placement = pos=(3,-12,-1) rot=(0.57735,0.57735,0.57735;2.0944rad)
  Sketch = -> Sketch012
  Type = 0
FEATURE [Part::Cut] Cut085
  Base = -> Pad005
  Tool = -> Pad007
FEATURE [Part::Cylinder] Cylinder056  label="Cilindro"
  Angle = 360
  Height = 10
  Placement = pos=(17.25,-4,120) rot=(1,0,0;1.5708rad)
  Radius = 10
FEATURE [Part::Cut] Cut086
  Base = -> Cut085
  Tool = -> Cylinder056
FEATURE [Part::Cylinder] Cylinder057  label="Cilindro001"
  Angle = 360
  Height = 13
  Placement = pos=(17.25,-6,120) rot=(1,0,0;1.5708rad)
  Radius = 3
FEATURE [Part::Cut] Cut087
  Base = -> Cut086
  Tool = -> Cylinder057
FEATURE [Part::Chamfer] Chamfer104
  Base = -> Cut087
  Edges = 1 edges r=1: [Edge10]
FEATURE [Part::Cylinder] Cylinder058  label="Cilindro002"
  Angle = 360
  Height = 22
  Placement = pos=(20.25,-32,125.75) rot=(0,1,0;1.5708rad)
  Radius = 3
FEATURE [Part::Cut] Cut088
  Base = -> Chamfer104
  Tool = -> Cylinder058
FEATURE [Part::Cylinder] Cylinder059  label="Cilindro003"
  Angle = 360
  Height = 22
  Placement = pos=(20.25,-34,132.75) rot=(0,1,0;1.5708rad)
  Radius = 1.25
FEATURE [Part::Cylinder] Cylinder060  label="Cilindro004"
  Angle = 360
  Height = 22
  Placement = pos=(20.25,-30,118.75) rot=(0,1,0;1.5708rad)
  Radius = 1.25
FEATURE [Part::Cylinder] Cylinder061  label="Cilindro005"
  Angle = 360
  Height = 22
  Placement = pos=(20.25,-38,124.25) rot=(0,1,0;1.5708rad)
  Radius = 1.25
FEATURE [Part::Cylinder] Cylinder062  label="Cilindro006"
  Angle = 360
  Height = 22
  Placement = pos=(20.25,-26,127.25) rot=(0,1,0;1.5708rad)
  Radius = 1.25
FEATURE [Part::MultiFuse] Fusion046
  Shapes = -> [Cylinder059,Cylinder061,Cylinder062,Cylinder060]
FEATURE [Part::Cylinder] Cylinder063  label="Cilindro007"
  Angle = 360
  Height = 22
  Placement = pos=(20.25,-34,132.75) rot=(0,1,0;1.5708rad)
  Radius = 1.25
FEATURE [Part::Cylinder] Cylinder064  label="Cilindro008"
  Angle = 360
  Height = 22
  Placement = pos=(20.25,-30,118.75) rot=(0,1,0;1.5708rad)
  Radius = 1.25
FEATURE [Part::Cylinder] Cylinder065  label="Cilindro009"
  Angle = 360
  Height = 22
  Placement = pos=(20.25,-38,124.25) rot=(0,1,0;1.5708rad)
  Radius = 1.25
FEATURE [Part::Cylinder] Cylinder066  label="Cilindro010"
  Angle = 360
  Height = 22
  Placement = pos=(20.25,-26,127.25) rot=(0,1,0;1.5708rad)
  Radius = 1.25
FEATURE [Part::MultiFuse] Fusion047
  Placement = pos=(114.108,21,33.6462) rot=(0.280624,-0.280624,-0.917878;1.65638rad)
  Shapes = -> [Cylinder063,Cylinder065,Cylinder066,Cylinder064]
FEATURE [Part::Cut] Cut089
  Base = -> Cut088
  Tool = -> Fusion047
FEATURE [Part::Cut] Cut090
  Base = -> Cut089
  Tool = -> Fusion046
FEATURE [Part::Cylinder] Cylinder067  label="Cilindro011"
  Angle = 360
  Height = 22
  Placement = pos=(-4.75,-32,125.75) rot=(0,1,0;1.5708rad)
  Radius = 1.75
FEATURE [Part::Cut] Cut091  label="shoulder-src"
  Base = -> Cut090
  Tool = -> Cylinder067
FEATURE [Part::FeaturePython] Clone011  label="microservo003"  # Draft clone (typed FeaturePython)
  Objects = -> [Clone009]
  Placement = pos=(-171,51.5,122.5) rot=(0.57735,-0.57735,0.57735;2.0944rad)
  Scale = (1,1,1)
FEATURE [Part::Box] Box054  label="Cubo004"
  Height = 56
  Length = 19
  Placement = pos=(4,98,80) rot=(0,0,1;0rad)
  Width = 15
FEATURE [Part::Cylinder] Cylinder073  label="Cilindro014"
  Angle = 360
  Height = 32
  Placement = pos=(8,90,84) rot=(-1,0,0;1.5708rad)
  Radius = 1.75
FEATURE [Part::Cylinder] Cylinder074  label="Cilindro015"
  Angle = 360
  Height = 32
  Placement = pos=(18,90,84) rot=(-1,0,0;1.5708rad)
  Radius = 1.75
FEATURE [Part::MultiFuse] Fusion056
  Shapes = -> [Cylinder074,Cylinder073]
FEATURE [Part::Cut] Cut098
  Base = -> Box054
  Tool = -> Fusion056
FEATURE [Sketcher::SketchObject] Sketch015
  Placement = pos=(38,-16,143.25) rot=(0,1,0;1.5708rad)
  sketch-geometry (7):
    g0: Circle CenterX=37 CenterY=120 CenterZ=0 NormalX=0 NormalY=0 NormalZ=1 Radius=1
    g1: Circle CenterX=9.5 CenterY=120 CenterZ=0 NormalX=0 NormalY=0 NormalZ=1 Radius=1
    g2: LineSegment StartX=35.25 StartY=126.5 StartZ=0 EndX=11.25 EndY=126.5 EndZ=0
    g3: LineSegment StartX=11.25 StartY=126.5 StartZ=0 EndX=11.25 EndY=113.5 EndZ=0
    g4: LineSegment StartX=11.25 StartY=113.5 StartZ=0 EndX=35.25 EndY=113.5 EndZ=0
    g5: LineSegment StartX=35.25 StartY=113.5 StartZ=0 EndX=35.25 EndY=126.5 EndZ=0
    g6: LineSegment [constr] StartX=9.5 StartY=120 StartZ=0 EndX=37 EndY=120 EndZ=0
  constraints (20):
    c: Coincident(g2,g3)
    c: Coincident(g3,g4)
    c: Coincident(g4,g5)
    c: Coincident(g5,g2)
    c: Horizontal(g2)
    c: Horizontal(g4)
    c: Vertical(g3)
    c: Vertical(g5)
    c: Distance(g2) = 24
    c: Distance(g5) = 13
    c: Radius(g1) = 1
    c: Equal(g1,g0)
    c: Coincident(g0,g6)
    c: Coincident(g1,g6)
    c: Distance(g6) = 27.5
    c: Horizontal(g6)
    c: DistanceX(g-1,g1) = 9.5
    c: DistanceY(g1) = 120
    c: DistanceY(g1,g3) = -6.5
    c: DistanceX(g1,g2) = 1.75
FEATURE [PartDesign::Pad] Pad010
  Length = 30
  Length2 = 100
  Placement = pos=(38,-16,143.25) rot=(0,1,0;1.5708rad)
  Reversed = true
  Sketch = -> Sketch015
  Type = 0
FEATURE [Part::Cut] Cut099
  Base = -> Cut098
  Tool = -> Pad010
FEATURE [Part::Chamfer] Chamfer108
  Base = -> Cut099
  Edges = 2 edges r=3: [Edge2,Edge14]
FEATURE [Part::Cylinder] Cylinder075  label="Cilindro016"
  Angle = 360
  Height = 32
  Placement = pos=(-5,104,125.85) rot=(-0.57735,0.57735,-0.57735;2.0944rad)
  Radius = 1.75
FEATURE [Part::Prism] Prism001  label="Prisma"
  Circumradius = 3.3
  Height = 10
  Placement = pos=(6,104,125.85) rot=(-0.57735,0.57735,-0.57735;2.0944rad)
  Polygon = 6
FEATURE [Part::MultiFuse] Fusion057
  Shapes = -> [Prism001,Cylinder075]
FEATURE [Part::Cut] Cut100  label="arm-src"
  Base = -> Chamfer108
  Tool = -> Fusion057
FEATURE [Part::Box] Box057  label="Cube078"
  Height = 66
  Length = 76
  Placement = pos=(-21,-2,87) rot=(0,0,1;0rad)
  Width = 76
FEATURE [Part::Fillet] Fillet018013003
  Base = -> Box057
  Edges = 8 edges r=3.5: [Edge1,Edge2,Edge3,Edge5,Edge6,Edge7,Edge10,Edge12]
  Placement = pos=(0,0,-24) rot=(0,0,1;0rad)
FEATURE [Part::Cylinder] Cylinder078  label="Cylinder105"
  Angle = 360
  Height = 31
  Placement = pos=(-8.5,11,71.5) rot=(1,0,0;1.5708rad)
  Radius = 1.75
FEATURE [Part::Cylinder] Cylinder079  label="Cylinder106"
  Angle = 360
  Height = 31
  Placement = pos=(-8.5,80,71.5) rot=(1,0,0;1.5708rad)
  Radius = 1.75
FEATURE [Part::Cylinder] Cylinder080  label="Cylinder107"
  Angle = 360
  Height = 31
  Placement = pos=(-4,11,83.5) rot=(1,0,0;1.5708rad)
  Radius = 6
FEATURE [Part::Box] Box058  label="Cube079"
  Height = 11
  Length = 8
  Placement = pos=(-13.5,-13,95) rot=(0,0,1;0rad)
  Width = 24
FEATURE [Part::Cylinder] Cylinder083  label="Cylinder108"
  Angle = 360
  Height = 31
  Placement = pos=(-7,80,89.6) rot=(1,0,0;1.5708rad)
  Radius = 4
FEATURE [Part::Box] Box059  label="Cube080"
  Height = 49
  Length = 17
  Placement = pos=(-14,-2.5,75) rot=(0,0,1;0rad)
  Width = 77
FEATURE [Part::Fillet] Fillet018013005
  Base = -> Box059
  Edges = 12 edges r=2: [Edge1,Edge2,Edge3,Edge4,Edge5,Edge6,Edge7,Edge8,Edge9,Edge10,Edge11,Edge12]
FEATURE [Part::Box] Box060  label="Cubo007"
  Height = 63
  Length = 80
  Placement = pos=(-23,-4,68) rot=(0,0,1;0rad)
  Width = 80
FEATURE [Part::Cut] Cut103
  Base = -> Box060
  Tool = -> Fillet018013003
FEATURE [Part::MultiFuse] Fusion061
  Shapes = -> [Box058,Cylinder080,Cylinder078,Fillet018013005,Cylinder083,Cylinder079]
FEATURE [Part::Cut] Cut104
  Base = -> Cut103
  Tool = -> Fusion061
FEATURE [Sketcher::SketchObject] Sketch017
  Placement = pos=(-0.25,-35,0) rot=(1,0,0;1.5708rad)
  sketch-geometry (7):
    g0: Circle CenterX=37 CenterY=120 CenterZ=0 NormalX=0 NormalY=0 NormalZ=1 Radius=1.2
    g1: Circle CenterX=9.5 CenterY=120 CenterZ=0 NormalX=0 NormalY=0 NormalZ=1 Radius=1.2
    g2: LineSegment StartX=35.25 StartY=126.5 StartZ=0 EndX=11.25 EndY=126.5 EndZ=0
    g3: LineSegment StartX=11.25 StartY=126.5 StartZ=0 EndX=11.25 EndY=113.5 EndZ=0
    g4: LineSegment StartX=11.25 StartY=113.5 StartZ=0 EndX=35.25 EndY=113.5 EndZ=0
    g5: LineSegment StartX=35.25 StartY=113.5 StartZ=0 EndX=35.25 EndY=126.5 EndZ=0
    g6: LineSegment [constr] StartX=9.5 StartY=120 StartZ=0 EndX=37 EndY=120 EndZ=0
  constraints (20):
    c: Coincident(g2,g3)
    c: Coincident(g3,g4)
    c: Coincident(g4,g5)
    c: Coincident(g5,g2)
    c: Horizontal(g2)
    c: Horizontal(g4)
    c: Vertical(g3)
    c: Vertical(g5)
    c: Distance(g2) = 24
    c: Distance(g5) = 13
    c: Radius(g1) = 1.2
    c: Equal(g1,g0)
    c: Coincident(g0,g6)
    c: Coincident(g1,g6)
    c: Distance(g6) = 27.5
    c: Horizontal(g6)
    c: DistanceX(g-1,g1) = 9.5
    c: DistanceY(g1) = 120
    c: DistanceY(g1,g3) = -6.5
    c: DistanceX(g1,g2) = 1.75
FEATURE [PartDesign::Pad] Pad012
  Length = 140
  Length2 = 100
  Placement = pos=(-0.25,-35,0) rot=(1,0,0;1.5708rad)
  Reversed = true
  Sketch = -> Sketch017
  Type = 0
FEATURE [Part::Box] Box061  label="Cubo008"
  Height = 4
  Length = 14
  Placement = pos=(11,75.5,109) rot=(0,0,1;0rad)
  Width = 3
FEATURE [Part::Box] Box062  label="Cubo009"
  Height = 4
  Length = 14
  Placement = pos=(11,75.5,127) rot=(0,0,1;0rad)
  Width = 3
FEATURE [Part::Box] Box063  label="Cubo010"
  Height = 4
  Length = 14
  Placement = pos=(11,-6.5,109) rot=(0,0,1;0rad)
  Width = 3
FEATURE [Part::Box] Box064  label="Cubo011"
  Height = 4
  Length = 14
  Placement = pos=(11,-6.5,127) rot=(0,0,1;0rad)
  Width = 3
FEATURE [Part::Cut] Cut105
  Base = -> Cut104
  Tool = -> Pad012
FEATURE [Part::MultiFuse] Fusion062
  Shapes = -> [Cut105,Box062,Box061,Box063,Box064]
FEATURE [Part::Fillet] Fillet018013006  label="prebody"
  Base = -> Fusion062
  Edges = 8 edges r=1: [Edge2,Edge4,Edge64,Edge66,Edge160,Edge165,Edge170,Edge174]
FEATURE [Part::FeaturePython] Clone020  label="right-shoulder"  # Draft clone (typed FeaturePython)
  Objects = -> [Cut091]
  Placement = pos=(-275,70,2.5) rot=(0,0,-1;1.5708rad)
  Scale = (1,1,1)
FEATURE [Part::Mirroring] Part__Mirroring007012  label="left-shoulder"
  Base = (0,0,0)
  Normal = (0,1,0)
  Placement = pos=(-478,0,0) rot=(0,0,1;3.14159rad)
  Source = -> Clone020
FEATURE [Part::FeaturePython] Clone022  label="head-servo"  # Draft clone (typed FeaturePython)
  Objects = -> [Clone009]
  Placement = pos=(-239,46.75,151) rot=(0.707107,0.707107,0;3.14159rad)
  Scale = (1,1,1)
FEATURE [Part::Feature] Pocket005  label="shaft-drill001"
  Placement = pos=(-171,34.6,128.25) rot=(1,0,0;1.5708rad)
  shape: bbox 18.7 x 4.1 x 18.7 mm, 22 faces (baked)
FEATURE [Part::Cylinder] Cylinder084  label="Cilindro019"
  Angle = 360
  Height = 13
  Placement = pos=(17.25,-6,120) rot=(1,0,0;1.5708rad)
  Radius = 3
FEATURE [Part::Cylinder] Cylinder085  label="Cilindro020"
  Angle = 360
  Height = 22
  Placement = pos=(20.25,-34,132.75) rot=(0,1,0;1.5708rad)
  Radius = 1.25
FEATURE [Part::Cylinder] Cylinder086  label="Cilindro021"
  Angle = 360
  Height = 22
  Placement = pos=(20.25,-30,118.75) rot=(0,1,0;1.5708rad)
  Radius = 1.25
FEATURE [Part::Cylinder] Cylinder087  label="Cilindro022"
  Angle = 360
  Height = 22
  Placement = pos=(20.25,-38,124.25) rot=(0,1,0;1.5708rad)
  Radius = 1.25
FEATURE [Part::Cylinder] Cylinder088  label="Cilindro023"
  Angle = 360
  Height = 22
  Placement = pos=(20.25,-26,127.25) rot=(0,1,0;1.5708rad)
  Radius = 1.25
FEATURE [Part::MultiFuse] Fusion063
  Placement = pos=(114.108,21,33.6462) rot=(0.280624,-0.280624,-0.917878;1.65638rad)
  Shapes = -> [Cylinder085,Cylinder087,Cylinder088,Cylinder086]
FEATURE [Part::MultiFuse] Fusion064
  Placement = pos=(-256.25,172.75,144) rot=(1,0,0;1.5708rad)
  Shapes = -> [Fusion063,Cylinder084]
FEATURE [Part::Box] Box065  label="Cubo"
  Height = 4
  Length = 10
  Placement = pos=(13,-11,104) rot=(0,0,1;0rad)
  Width = 94
FEATURE [Part::Cut] Cut107  label="body-src"
  Base = -> Fillet018013006
  Tool = -> Box065
FEATURE [Part::FeaturePython] Clone024  label="Clone of body-src"  # Draft clone (typed FeaturePython)
  Objects = -> [Cut107]
  Placement = pos=(-275,70,2) rot=(0,0,-1;1.5708rad)
  Scale = (1,1,1)
FEATURE [Part::Cut] Cut108
  Base = -> Clone024
  Tool = -> Fusion064
FEATURE [Part::Box] Box066  label="Cubo012"
  Height = 10
  Length = 10
  Placement = pos=(-244,64,124) rot=(0,0,1;0rad)
  Width = 4
FEATURE [Part::Cut] Cut109  label="body-yaw-head"
  Base = -> Cut108
  Tool = -> Box066
FEATURE [Part::Feature] Compound  label="Servo-Futaba-3003-ready002"
  Placement = pos=(-203,69.69,14.95) rot=(0,0.707107,-0.707107;3.14159rad)
  shape: bbox 57.75 x 41.74 x 20 mm, 378 faces, 4 solids (baked)
FEATURE [Part::Feature] Chamfer109  label="ISO4762_Hex_screw-M3x020"
  Placement = pos=(-227.45,37.49,20) rot=(0.57735,0.57735,-0.57735;2.0944rad)
  shape: bbox 5.5 x 19 x 5.5 mm, 16 faces (baked)
FEATURE [Part::Feature] Chamfer110  label="ISO4762_Hex_screw-M3x023"
  Placement = pos=(-227.45,37.49,10) rot=(0.57735,0.57735,-0.57735;2.0944rad)
  shape: bbox 5.5 x 19 x 5.5 mm, 16 faces (baked)
FEATURE [Part::Feature] Chamfer111  label="ISO4032-Hex-Nut-M008"
  Placement = pos=(-227.45,48.69,10) rot=(0,0,1;0rad)
  shape: bbox 6.35 x 2.4 x 6.35 mm, 29 faces (baked)
FEATURE [Part::Feature] Chamfer112  label="ISO4032-Hex-Nut-M007"
  Placement = pos=(-227.45,48.49,20) rot=(0,0,1;0rad)
  shape: bbox 6.35 x 2.4 x 6.35 mm, 29 faces (baked)
FEATURE [Part::Feature] Chamfer113  label="ISO-10642-M3x011"
  Placement = pos=(-212.45,70.2132,15) rot=(0.57735,0.57735,-0.57735;2.0944rad)
  shape: bbox 6.046 x 10 x 6.046 mm, 25 faces (baked)
FEATURE [Part::Feature] Chamfer114  label="ISO4762_Hex_screw-M3x022"
  Placement = pos=(-178.45,37.49,20) rot=(0.57735,0.57735,-0.57735;2.0944rad)
  shape: bbox 5.5 x 19 x 5.5 mm, 16 faces (baked)
FEATURE [Part::Feature] Chamfer115  label="ISO4032-Hex-Nut-M010"
  Placement = pos=(-178.45,48.49,20) rot=(0,0,1;0rad)
  shape: bbox 6.35 x 2.4 x 6.35 mm, 29 faces (baked)
FEATURE [Part::Feature] Chamfer116  label="ISO4032-Hex-Nut-M009"
  Placement = pos=(-178.45,48.49,10) rot=(0,0,1;0rad)
  shape: bbox 6.35 x 2.4 x 6.35 mm, 29 faces (baked)
FEATURE [Part::Feature] Chamfer117  label="ISO4762_Hex_screw-M3x021"
  Placement = pos=(-178.45,37.49,10) rot=(0.57735,0.57735,-0.57735;2.0944rad)
  shape: bbox 5.5 x 19 x 5.5 mm, 16 faces (baked)
FEATURE [Part::Feature] Chamfer118  label="ISO-10642-M3x10"
  Placement = pos=(-265.35,70.0132,15) rot=(0.57735,0.57735,-0.57735;2.0944rad)
  shape: bbox 6.046 x 10 x 6.046 mm, 25 faces (baked)
FEATURE [Part::Feature] Chamfer119  label="ISO4032-Hex-Nut-M3"
  Placement = pos=(-250.35,48.29,20) rot=(0,0,1;0rad)
  shape: bbox 6.35 x 2.4 x 6.35 mm, 29 faces (baked)
FEATURE [Part::Feature] Chamfer120  label="ISO4032-Hex-Nut-M004"
  Placement = pos=(-250.35,47.69,10) rot=(0,0,1;0rad)
  shape: bbox 6.35 x 2.4 x 6.35 mm, 29 faces (baked)
FEATURE [Part::Feature] Chamfer121  label="ISO4032-Hex-Nut-M005"
  Placement = pos=(-299.35,47.69,20) rot=(0,0,1;0rad)
  shape: bbox 6.35 x 2.4 x 6.35 mm, 29 faces (baked)
FEATURE [Part::Feature] Chamfer122  label="ISO4032-Hex-Nut-M006"
  Placement = pos=(-299.35,47.69,10) rot=(0,0,1;0rad)
  shape: bbox 6.35 x 2.4 x 6.35 mm, 29 faces (baked)
FEATURE [Part::Feature] Chamfer123  label="ISO4762_Hex_screw-M3x16"
  Placement = pos=(-299.35,37.19,20) rot=(0.57735,0.57735,-0.57735;2.0944rad)
  shape: bbox 5.5 x 19 x 5.5 mm, 16 faces (baked)
FEATURE [Part::Feature] Compound001  label="Servo-Futaba-3003-ready001"
  Placement = pos=(-274.9,69.49,14.95) rot=(1,0,0;1.5708rad)
  shape: bbox 57.75 x 41.74 x 20 mm, 378 faces, 4 solids (baked)
FEATURE [Part::Feature] Chamfer124  label="ISO4762_Hex_screw-M3x017"
  Placement = pos=(-299.35,37.29,10) rot=(0.57735,0.57735,-0.57735;2.0944rad)
  shape: bbox 5.5 x 19 x 5.5 mm, 16 faces (baked)
FEATURE [Part::Feature] Chamfer125  label="ISO4762_Hex_screw-M3x018"
  Placement = pos=(-250.35,37.29,10) rot=(0.57735,0.57735,-0.57735;2.0944rad)
  shape: bbox 5.5 x 19 x 5.5 mm, 16 faces (baked)
FEATURE [Part::Feature] Chamfer126  label="ISO4762_Hex_screw-M3x019"
  Placement = pos=(-250.35,37.29,20) rot=(0.57735,0.57735,-0.57735;2.0944rad)
  shape: bbox 5.5 x 19 x 5.5 mm, 16 faces (baked)
FEATURE [Part::Feature] Fillet018013007  label="rounded-horn003"
  Placement = pos=(-265.45,52.9,64.75) rot=(-0.57735,0.57735,-0.57735;2.0944rad)
  shape: bbox 21 x 21 x 6.2 mm, 65 faces (baked)
FEATURE [Part::Feature] Fillet018013008  label="horn-screw009"
  Placement = pos=(-265.45,45.45,59.15) rot=(0,0.707107,-0.707107;3.14159rad)
  shape: bbox 4.8 x 4.8 x 5.5 mm, 21 faces (baked)
FEATURE [Part::Feature] Fillet018013009  label="horn-screw010"
  Placement = pos=(-272.9,55.245,59.15) rot=(0,0.707107,-0.707107;3.14159rad)
  shape: bbox 4.8 x 4.8 x 5.5 mm, 21 faces (baked)
FEATURE [Part::Feature] Fillet018013010  label="horn-screw011"
  Placement = pos=(-258,55.995,59.15) rot=(0,0.707107,-0.707107;3.14159rad)
  shape: bbox 4.8 x 4.8 x 5.5 mm, 21 faces (baked)
FEATURE [Part::Feature] Fillet018013011  label="rounded-horn002"
  Placement = pos=(-265.45,31.4,14.95) rot=(0.707107,0,-0.707107;3.14159rad)
  shape: bbox 21 x 6.2 x 21 mm, 65 faces (baked)
FEATURE [Part::Feature] Fillet018013012  label="horn-screw006"
  Placement = pos=(-265.45,25.8,22.4) rot=(0.707107,0,0.707107;3.14159rad)
  shape: bbox 4.8 x 5.5 x 4.8 mm, 21 faces (baked)
FEATURE [Part::Feature] Fillet018013013  label="horn-screw007"
  Placement = pos=(-258,25.8,11.855) rot=(0.707107,0,0.707107;3.14159rad)
  shape: bbox 4.8 x 5.5 x 4.8 mm, 21 faces (baked)
FEATURE [Part::Feature] Fillet018013014  label="horn-screw008"
  Placement = pos=(-272.9,25.8,11.855) rot=(0.707107,0,0.707107;3.14159rad)
  shape: bbox 4.8 x 5.5 x 4.8 mm, 21 faces (baked)
FEATURE [Part::Feature] Cut110  label="Shaft-bolt001"
  Placement = pos=(-265.402,52.9083,67.75) rot=(0.707107,-0.707107,0;3.14159rad)
  shape: bbox 5.38 x 5.38 x 9.391 mm, 18 faces (baked)
FEATURE [Part::Feature] Cut111  label="Shaft-bolt002"
  Placement = pos=(-212.402,52.9083,67.75) rot=(0.707107,-0.707107,0;3.14159rad)
  shape: bbox 5.38 x 5.38 x 9.391 mm, 18 faces (baked)
FEATURE [Part::Feature] Fillet018013015  label="horn-screw005"
  Placement = pos=(-219.9,26,11.855) rot=(0.707107,0,0.707107;3.14159rad)
  shape: bbox 4.8 x 5.5 x 4.8 mm, 21 faces (baked)
FEATURE [Part::Feature] Fillet018013016  label="horn-screw004"
  Placement = pos=(-212.45,26,22.4) rot=(0.707107,0,0.707107;3.14159rad)
  shape: bbox 4.8 x 5.5 x 4.8 mm, 21 faces (baked)
FEATURE [Part::Feature] Fillet018013017  label="horn-screw003"
  Placement = pos=(-205,26,11.855) rot=(0.707107,0,0.707107;3.14159rad)
  shape: bbox 4.8 x 5.5 x 4.8 mm, 21 faces (baked)
FEATURE [Part::Feature] Fillet018013018  label="horn-screw002"
  Placement = pos=(-219.9,55.245,59.15) rot=(0,0.707107,-0.707107;3.14159rad)
  shape: bbox 4.8 x 4.8 x 5.5 mm, 21 faces (baked)
FEATURE [Part::Feature] Fillet018013019  label="horn-screw001"
  Placement = pos=(-212.45,45.45,59.15) rot=(0,0.707107,-0.707107;3.14159rad)
  shape: bbox 4.8 x 4.8 x 5.5 mm, 21 faces (baked)
FEATURE [Part::Feature] Fillet018013020  label="horn-screw"
  Placement = pos=(-205,55.995,59.15) rot=(0,0.707107,-0.707107;3.14159rad)
  shape: bbox 4.8 x 4.8 x 5.5 mm, 21 faces (baked)
FEATURE [Part::Feature] Fillet018013021  label="rounded-horn001"
  Placement = pos=(-212.45,52.9,64.75) rot=(-0.57735,0.57735,-0.57735;2.0944rad)
  shape: bbox 21 x 21 x 6.2 mm, 65 faces (baked)
FEATURE [Part::Feature] Fillet018013022  label="rounded-horn"
  Placement = pos=(-212.45,31.6,14.95) rot=(0.707107,0,-0.707107;3.14159rad)
  shape: bbox 21 x 6.2 x 21 mm, 65 faces (baked)
FEATURE [Part::Feature] Chamfer127  label="ISO4762_Hex_screw-M3x10"
  Placement = pos=(-246,80.8,113.94) rot=(0.57735,0.57735,-0.57735;2.0944rad)
  shape: bbox 5.5 x 13 x 5.5 mm, 16 faces (baked)
FEATURE [Part::Feature] Chamfer128  label="ISO4762_Hex_screw-M3x027"
  Placement = pos=(-246,80.8,93.94) rot=(0.57735,0.57735,-0.57735;2.0944rad)
  shape: bbox 5.5 x 13 x 5.5 mm, 16 faces (baked)
FEATURE [Part::Feature] Chamfer129  label="ISO4762_Hex_screw-M3x024"
  Placement = pos=(-226,80.8,113.94) rot=(0.57735,0.57735,-0.57735;2.0944rad)
  shape: bbox 5.5 x 13 x 5.5 mm, 16 faces (baked)
FEATURE [Part::Feature] Chamfer130  label="ISO4032-Hex-Nut-M012"
  Placement = pos=(-246,87.5,113.94) rot=(0,0,1;0rad)
  shape: bbox 6.35 x 2.4 x 6.35 mm, 29 faces (baked)
FEATURE [Part::Feature] Chamfer131  label="ISO4762_Hex_screw-M3x025"
  Placement = pos=(-246,80.8,93.94) rot=(0.57735,0.57735,-0.57735;2.0944rad)
  shape: bbox 5.5 x 13 x 5.5 mm, 16 faces (baked)
FEATURE [Part::Feature] Chamfer132  label="ISO4032-Hex-Nut-M013"
  Placement = pos=(-226,87.5,93.94) rot=(0,0,1;0rad)
  shape: bbox 6.35 x 2.4 x 6.35 mm, 29 faces (baked)
FEATURE [Part::Feature] Chamfer133  label="ISO4762_Hex_screw-M3x026"
  Placement = pos=(-226,80.8,93.94) rot=(0.57735,0.57735,-0.57735;2.0944rad)
  shape: bbox 5.5 x 13 x 5.5 mm, 16 faces (baked)
FEATURE [Part::Feature] Chamfer134  label="ISO4032-Hex-Nut-M014"
  Placement = pos=(-246,87.5,93.94) rot=(0,0,1;0rad)
  shape: bbox 6.35 x 2.4 x 6.35 mm, 29 faces (baked)
FEATURE [Part::Feature] Chamfer135  label="ISO4032-Hex-Nut-M011"
  Placement = pos=(-226,87.5,113.94) rot=(0,0,1;0rad)
  shape: bbox 6.35 x 2.4 x 6.35 mm, 29 faces (baked)
FEATURE [Part::Feature] Chamfer136  label="ISO4032-Hex-Nut-M020"
  Placement = pos=(-207.5,19,77.04) rot=(0.57735,-0.57735,-0.57735;2.0944rad)
  shape: bbox 6.35 x 6.35 x 2.4 mm, 29 faces (baked)
FEATURE [Part::Feature] Chamfer137  label="ISO4762_Hex_screw-M3x033"
  Placement = pos=(-217.5,19,68.54) rot=(0.707107,-0.707107,0;3.14159rad)
  shape: bbox 5.5 x 5.5 x 15 mm, 16 faces (baked)
FEATURE [Part::Feature] Chamfer138  label="ISO4762_Hex_screw-M3x030"
  Placement = pos=(-270.5,68,68.54) rot=(0.707107,-0.707107,0;3.14159rad)
  shape: bbox 5.5 x 5.5 x 15 mm, 16 faces (baked)
FEATURE [Part::Feature] Chamfer139  label="ISO4762_Hex_screw-M3x031"
  Placement = pos=(-217.5,68,68.54) rot=(0.707107,-0.707107,0;3.14159rad)
  shape: bbox 5.5 x 5.5 x 15 mm, 16 faces (baked)
FEATURE [Part::Feature] Chamfer140  label="ISO4762_Hex_screw-M3x032"
  Placement = pos=(-207.5,68,68.54) rot=(0.707107,-0.707107,0;3.14159rad)
  shape: bbox 5.5 x 5.5 x 15 mm, 16 faces (baked)
FEATURE [Part::Feature] Chamfer141  label="ISO4032-Hex-Nut-M019"
  Placement = pos=(-217.5,19,77.04) rot=(0.57735,-0.57735,-0.57735;2.0944rad)
  shape: bbox 6.35 x 6.35 x 2.4 mm, 29 faces (baked)
FEATURE [Part::Feature] Chamfer142  label="ISO4762_Hex_screw-M3x029"
  Placement = pos=(-260.5,68,68.54) rot=(0.707107,-0.707107,0;3.14159rad)
  shape: bbox 5.5 x 5.5 x 15 mm, 16 faces (baked)
FEATURE [Part::Feature] Chamfer143  label="ISO4032-Hex-Nut-M018"
  Placement = pos=(-270.5,19,77.04) rot=(0.57735,-0.57735,-0.57735;2.0944rad)
  shape: bbox 6.35 x 6.35 x 2.4 mm, 29 faces (baked)
FEATURE [Part::Feature] Chamfer144  label="ISO4762_Hex_screw-M3x12"
  Placement = pos=(-270.5,19,68.54) rot=(0.707107,-0.707107,0;3.14159rad)
  shape: bbox 5.5 x 5.5 x 15 mm, 16 faces (baked)
FEATURE [Part::Feature] Chamfer145  label="ISO4032-Hex-Nut-M017"
  Placement = pos=(-260.5,68,77.04) rot=(0.57735,-0.57735,-0.57735;2.0944rad)
  shape: bbox 6.35 x 6.35 x 2.4 mm, 29 faces (baked)
FEATURE [Part::Feature] Chamfer146  label="ISO4032-Hex-Nut-M023"
  Placement = pos=(-272,78.5,73.94) rot=(0,0,-1;1.5708rad)
  shape: bbox 2.4 x 6.35 x 6.35 mm, 29 faces (baked)
FEATURE [Part::Feature] Chamfer147  label="ISO4762_Hex_screw-M3x028"
  Placement = pos=(-260.5,19,68.54) rot=(0.707107,-0.707107,0;3.14159rad)
  shape: bbox 5.5 x 5.5 x 15 mm, 16 faces (baked)
FEATURE [Part::Feature] Chamfer148  label="ISO4032-Hex-Nut-M022"
  Placement = pos=(-217.5,68,77.04) rot=(0.57735,-0.57735,-0.57735;2.0944rad)
  shape: bbox 6.35 x 6.35 x 2.4 mm, 29 faces (baked)
FEATURE [Part::Feature] Chamfer149  label="ISO4032-Hex-Nut-M021"
  Placement = pos=(-207.5,68,77.04) rot=(0.57735,-0.57735,-0.57735;2.0944rad)
  shape: bbox 6.35 x 6.35 x 2.4 mm, 29 faces (baked)
FEATURE [Part::Feature] Compound002  label="Servo-Futaba-3003-ready003"
  Placement = pos=(-265.45,43.45,102.84) rot=(0.707107,0.707107,0;3.14159rad)
  shape: bbox 20 x 57.75 x 41.74 mm, 378 faces, 4 solids (baked)
FEATURE [Part::Feature] Chamfer150  label="ISO4032-Hex-Nut-M015"
  Placement = pos=(-260.5,19,77.04) rot=(0.57735,-0.57735,-0.57735;2.0944rad)
  shape: bbox 6.35 x 6.35 x 2.4 mm, 29 faces (baked)
FEATURE [Part::Feature] Compound003  label="Servo-Futaba-3003-ready004"
  Placement = pos=(-212.45,43.45,102.84) rot=(0.707107,0.707107,0;3.14159rad)
  shape: bbox 20 x 57.75 x 41.74 mm, 378 faces, 4 solids (baked)
FEATURE [Part::Feature] Chamfer151  label="ISO4762_Hex_screw-M3x034"
  Placement = pos=(-207.5,19,68.54) rot=(0.707107,-0.707107,0;3.14159rad)
  shape: bbox 5.5 x 5.5 x 15 mm, 16 faces (baked)
FEATURE [Part::Feature] Chamfer152  label="ISO4032-Hex-Nut-M016"
  Placement = pos=(-270.5,68,77.04) rot=(0.57735,-0.57735,-0.57735;2.0944rad)
  shape: bbox 6.35 x 6.35 x 2.4 mm, 29 faces (baked)
FEATURE [Part::Feature] Chamfer153  label="ISO4032-Hex-Nut-M024"
  Placement = pos=(-208.2,78.5,73.94) rot=(0,0,-1;1.5708rad)
  shape: bbox 2.4 x 6.35 x 6.35 mm, 29 faces (baked)
FEATURE [Part::Feature] Chamfer154  label="ISO4762_Hex_screw-M3x035"
  Placement = pos=(-307,70.9,128.25) rot=(-1,0,0;1.5708rad)
  shape: bbox 5.5 x 13 x 5.5 mm, 16 faces (baked)
FEATURE [Part::Feature] Chamfer155  label="ISO4762_Hex_screw-M3x036"
  Placement = pos=(-278.9,78.5,73.94) rot=(0.57735,0.57735,-0.57735;4.18879rad)
  shape: bbox 13 x 5.5 x 5.5 mm, 16 faces (baked)
FEATURE [Part::Feature] Pocket007  label="shaft-drill003"
  Placement = pos=(-239,52.75,134.5) rot=(0,1,0;3.14159rad)
  shape: bbox 18.7 x 18.7 x 4.1 mm, 22 faces (baked)
FEATURE [Part::Feature] Pocket008  label="shaft-drill004"
  Placement = pos=(-307,34.6,128.25) rot=(1,0,0;1.5708rad)
  shape: bbox 18.7 x 4.1 x 18.7 mm, 22 faces (baked)
FEATURE [Part::Feature] Chamfer156  label="ISO4762_Hex_screw-M3x037"
  Placement = pos=(-199.1,78.5,73.94) rot=(-0.57735,0.57735,-0.57735;2.0944rad)
  shape: bbox 13 x 5.5 x 5.5 mm, 16 faces (baked)
FEATURE [Part::Feature] Chamfer157  label="ISO4032-Hex-Nut-M025"
  Placement = pos=(-171,61.5,128.25) rot=(0,1,0;0.523599rad)
  shape: bbox 6.35 x 2.4 x 6.35 mm, 29 faces (baked)
FEATURE [Part::Feature] Fillet018013023  label="horn-screw012"
  Placement = pos=(-173,29,121.25) rot=(0.707107,0,0.707107;3.14159rad)
  shape: bbox 4.8 x 5.5 x 4.8 mm, 21 faces (baked)
FEATURE [Part::Feature] Fillet018013024  label="horn-screw013"
  Placement = pos=(-169,29,135.25) rot=(0.707107,0,0.707107;3.14159rad)
  shape: bbox 4.8 x 5.5 x 4.8 mm, 21 faces (baked)
FEATURE [Part::Feature] Fillet018013025  label="horn-screw014"
  Placement = pos=(-171,45.2,108.7) rot=(0.707107,0,0.707107;3.14159rad)
  shape: bbox 4.8 x 5.5 x 4.8 mm, 21 faces (baked)
FEATURE [Part::Feature] Fillet018013026  label="horn-screw015"
  Placement = pos=(-165,29,126.75) rot=(0.707107,0,0.707107;3.14159rad)
  shape: bbox 4.8 x 5.5 x 4.8 mm, 21 faces (baked)
FEATURE [Part::Feature] Fillet018013027  label="horn-screw016"
  Placement = pos=(-171,45.2,136.3) rot=(0.707107,0,0.707107;3.14159rad)
  shape: bbox 4.8 x 5.5 x 4.8 mm, 21 faces (baked)
FEATURE [Part::Feature] Fillet018013028  label="horn-screw017"
  Placement = pos=(-177,29,129.75) rot=(0.707107,0,0.707107;3.14159rad)
  shape: bbox 4.8 x 5.5 x 4.8 mm, 21 faces (baked)
FEATURE [Part::Feature] Fillet018013029  label="horn-screw018"
  Placement = pos=(-234.854,48.1478,131) rot=(-1,0,0;1.5708rad)
  shape: bbox 4.8 x 4.8 x 5.5 mm, 21 faces (baked)
FEATURE [Part::Feature] Fillet018013030  label="horn-screw019"
  Placement = pos=(-307,45.2,108.7) rot=(0.707107,0,0.707107;3.14159rad)
  shape: bbox 4.8 x 5.5 x 4.8 mm, 21 faces (baked)
FEATURE [Part::Feature] Fillet018013031  label="horn-screw020"
  Placement = pos=(-309,29,135.25) rot=(0.707107,0,0.707107;3.14159rad)
  shape: bbox 4.8 x 5.5 x 4.8 mm, 21 faces (baked)
FEATURE [Part::Feature] Fillet018013032  label="horn-screw021"
  Placement = pos=(-305,29,121.25) rot=(0.707107,0,0.707107;3.14159rad)
  shape: bbox 4.8 x 5.5 x 4.8 mm, 21 faces (baked)
FEATURE [Part::Feature] Fillet018013033  label="horn-screw022"
  Placement = pos=(-244.562,48.0616,131) rot=(-1,0,0;1.5708rad)
  shape: bbox 4.8 x 4.8 x 5.5 mm, 21 faces (baked)
FEATURE [Part::Feature] Fillet018013034  label="horn-screw023"
  Placement = pos=(-233.417,57.4313,131) rot=(-1,0,0;1.5708rad)
  shape: bbox 4.8 x 4.8 x 5.5 mm, 21 faces (baked)
FEATURE [Part::Feature] Fillet018013035  label="horn-screw024"
  Placement = pos=(-301,29,129.75) rot=(0.707107,0,0.707107;3.14159rad)
  shape: bbox 4.8 x 5.5 x 4.8 mm, 21 faces (baked)
FEATURE [Part::Feature] Fillet018013036  label="horn-screw025"
  Placement = pos=(-307,45.2,136.3) rot=(0.707107,0,0.707107;3.14159rad)
  shape: bbox 4.8 x 5.5 x 4.8 mm, 21 faces (baked)
FEATURE [Part::Feature] Fillet018013037  label="horn-screw026"
  Placement = pos=(-313,29,126.75) rot=(0.707107,0,0.707107;3.14159rad)
  shape: bbox 4.8 x 5.5 x 4.8 mm, 21 faces (baked)
FEATURE [Part::Feature] Fillet018013038  label="horn-screw027"
  Placement = pos=(-243.125,57.3452,131) rot=(-1,0,0;1.5708rad)
  shape: bbox 4.8 x 4.8 x 5.5 mm, 21 faces (baked)
FEATURE [Part::Feature] Pocket009  label="shaft-drill005"
  Placement = pos=(-190.8,52.75,122.5) rot=(0,1,0;1.5708rad)
  shape: bbox 4.1 x 18.7 x 18.7 mm, 22 faces (baked)
FEATURE [Part::Feature] Pocket010  label="shaft-drill006"
  Placement = pos=(-287.2,52.75,122.5) rot=(0,-1,0;1.5708rad)
  shape: bbox 4.1 x 18.7 x 18.7 mm, 22 faces (baked)
FEATURE [Part::Feature] Fillet018013039  label="horn-screw028"
  Placement = pos=(-291.882,58.3121,127.188) rot=(0,0,1;1.5708rad)
  shape: bbox 5.5 x 4.8 x 4.8 mm, 21 faces (baked)
FEATURE [Part::Feature] Fillet018013040  label="horn-screw029"
  Placement = pos=(-291.882,56.8751,117.905) rot=(0,0,1;1.5708rad)
  shape: bbox 5.5 x 4.8 x 4.8 mm, 21 faces (baked)
FEATURE [Part::Feature] Fillet018013041  label="horn-screw030"
  Placement = pos=(-279,33.25,122) rot=(0,0,1;1.5708rad)
  shape: bbox 5.5 x 4.8 x 4.8 mm, 21 faces (baked)
FEATURE [Part::Feature] Fillet018013042  label="horn-screw031"
  Placement = pos=(-291.882,47.1673,117.819) rot=(0,0,1;1.5708rad)
  shape: bbox 5.5 x 4.8 x 4.8 mm, 21 faces (baked)
FEATURE [Part::Feature] Fillet018013043  label="horn-screw032"
  Placement = pos=(-199,60.75,122) rot=(0,0,-1;1.5708rad)
  shape: bbox 5.5 x 4.8 x 4.8 mm, 21 faces (baked)
FEATURE [Part::Feature] Fillet018013044  label="horn-screw033"
  Placement = pos=(-186.118,56.8751,117.905) rot=(0,0,-1;1.5708rad)
  shape: bbox 5.5 x 4.8 x 4.8 mm, 21 faces (baked)
FEATURE [Part::Feature] Fillet018013045  label="horn-screw034"
  Placement = pos=(-186.118,47.1673,117.819) rot=(0,0,-1;1.5708rad)
  shape: bbox 5.5 x 4.8 x 4.8 mm, 21 faces (baked)
FEATURE [Part::Feature] Fillet018013046  label="horn-screw035"
  Placement = pos=(-186.118,48.6043,127.102) rot=(0,0,-1;1.5708rad)
  shape: bbox 5.5 x 4.8 x 4.8 mm, 21 faces (baked)
FEATURE [Part::Feature] Fillet018013047  label="horn-screw036"
  Placement = pos=(-199,33.25,122) rot=(0,0,-1;1.5708rad)
  shape: bbox 5.5 x 4.8 x 4.8 mm, 21 faces (baked)
FEATURE [Part::Feature] Fillet018013048  label="horn-screw037"
  Placement = pos=(-186.118,58.3121,127.188) rot=(0,0,-1;1.5708rad)
  shape: bbox 5.5 x 4.8 x 4.8 mm, 21 faces (baked)
FEATURE [Part::Feature] Fillet018013049  label="horn-screw038"
  Placement = pos=(-279,60.75,122) rot=(0,0,1;1.5708rad)
  shape: bbox 5.5 x 4.8 x 4.8 mm, 21 faces (baked)
FEATURE [Part::Feature] Fillet018013050  label="horn-screw039"
  Placement = pos=(-291.882,48.6043,127.102) rot=(0,0,1;1.5708rad)
  shape: bbox 5.5 x 4.8 x 4.8 mm, 21 faces (baked)
FEATURE [Part::Feature] Chamfer158  label="ISO4762_Hex_screw-M3x038"
  Placement = pos=(-171,71,128.25) rot=(-1,0,0;1.5708rad)
  shape: bbox 5.5 x 13 x 5.5 mm, 16 faces (baked)
FEATURE [Part::Feature] Pocket012  label="top-cross001"
  Placement = pos=(-283.6,52.75,122.5) rot=(0,-1,0;1.5708rad)
  shape: bbox 6.2 x 3 x 3 mm, 18 faces (baked)
FEATURE [Part::Feature] Pocket013  label="top-cross002"
  Placement = pos=(-171,38.2,128.25) rot=(1,0,0;1.5708rad)
  shape: bbox 3 x 6.2 x 3 mm, 18 faces (baked)
FEATURE [Part::Feature] Pocket014  label="top-cross003"
  Placement = pos=(-194.4,52.75,122.5) rot=(0,1,0;1.5708rad)
  shape: bbox 6.2 x 3 x 3 mm, 18 faces (baked)
FEATURE [Part::Feature] Pocket015  label="top-cross004"
  Placement = pos=(-239,52.75,138.1) rot=(1,0,0;3.14159rad)
  shape: bbox 3 x 3 x 6.2 mm, 18 faces (baked)
FEATURE [Part::Feature] Pocket016  label="top-cross005"
  Placement = pos=(-307,38.2,128.25) rot=(1,0,0;1.5708rad)
  shape: bbox 3 x 6.2 x 3 mm, 18 faces (baked)
FEATURE [App::DocumentObjectGroup] Grupo001  label="generic-components"
  Group = -> [Compound,Chamfer109,Chamfer110,Chamfer111,Chamfer112,Chamfer113,Chamfer114,Chamfer115,Chamfer116,Chamfer117,Chamfer118,Chamfer119,Chamfer120,Chamfer121,Chamfer122,Chamfer123,Compound001,Chamfer124,Chamfer125,Chamfer126,Fillet018013007,Fillet018013008,Fillet018013009,Fillet018013010,Fillet018013011,Fillet018013012,Fillet018013013,Fillet018013014,Cut110,Cut111,Fillet018013015,Fillet018013016,+83 more]
FEATURE [Part::Feature] Cut112  label="pie-D001"
  Placement = pos=(-274.85,69.19,3) rot=(0,0,-1;1.5708rad)
  shape: bbox 58 x 72 x 24 mm, 84 faces (baked)
FEATURE [Part::Feature] Part__Mirroring007015  label="pie-I001"
  Placement = pos=(-202.95,69.39,2) rot=(0,0,-1;1.5708rad)
  shape: bbox 58 x 72 x 24 mm, 84 faces (baked)
FEATURE [Sketcher::SketchObject] Sketch018
  Placement = pos=(70,275,66) rot=(0.707107,0.707107,0;3.14159rad)
  sketch-geometry (20):
    g0: LineSegment StartX=-270.5 StartY=-17 StartZ=0 EndX=-260.5 EndY=-17 EndZ=0
    g1: LineSegment StartX=-260.5 StartY=-17 StartZ=0 EndX=-260.5 EndY=-21 EndZ=0
    g2: LineSegment StartX=-260.5 StartY=-21 StartZ=0 EndX=-270.5 EndY=-21 EndZ=0
    g3: LineSegment StartX=-270.5 StartY=-21 StartZ=0 EndX=-270.5 EndY=-17 EndZ=0
    g4: LineSegment StartX=-217.5 StartY=-17 StartZ=0 EndX=-207.5 EndY=-17 EndZ=0
    g5: LineSegment StartX=-207.5 StartY=-17 StartZ=0 EndX=-207.5 EndY=-21 EndZ=0
    g6: LineSegment StartX=-207.5 StartY=-21 StartZ=0 EndX=-217.5 EndY=-21 EndZ=0
    g7: LineSegment StartX=-217.5 StartY=-21 StartZ=0 EndX=-217.5 EndY=-17 EndZ=0
    g8: LineSegment StartX=-270.5 StartY=-66 StartZ=0 EndX=-260.5 EndY=-66 EndZ=0
    g9: LineSegment StartX=-260.5 StartY=-66 StartZ=0 EndX=-260.5 EndY=-70 EndZ=0
    g10: LineSegment StartX=-260.5 StartY=-70 StartZ=0 EndX=-270.5 EndY=-70 EndZ=0
    g11: LineSegment StartX=-270.5 StartY=-70 StartZ=0 EndX=-270.5 EndY=-66 EndZ=0
    g12: LineSegment StartX=-217.5 StartY=-66 StartZ=0 EndX=-207.5 EndY=-66 EndZ=0
    g13: LineSegment StartX=-207.5 StartY=-66 StartZ=0 EndX=-207.5 EndY=-70 EndZ=0
    g14: LineSegment StartX=-207.5 StartY=-70 StartZ=0 EndX=-217.5 EndY=-70 EndZ=0
    g15: LineSegment StartX=-217.5 StartY=-70 StartZ=0 EndX=-217.5 EndY=-66 EndZ=0
    g16: LineSegment [constr] StartX=-260.5 StartY=-21 StartZ=0 EndX=-217.5 EndY=-21 EndZ=0
    g17: LineSegment [constr] StartX=-217.5 StartY=-21 StartZ=0 EndX=-217.5 EndY=-66 EndZ=0
    g18: LineSegment [constr] StartX=-217.5 StartY=-66 StartZ=0 EndX=-260.5 EndY=-66 EndZ=0
    g19: LineSegment [constr] StartX=-260.5 StartY=-66 StartZ=0 EndX=-260.5 EndY=-21 EndZ=0
  constraints (56):
    c: Coincident(g0,g1)
    c: Coincident(g1,g2)
    c: Coincident(g2,g3)
    c: Coincident(g3,g0)
    c: Horizontal(g0)
    c: Horizontal(g2)
    c: Vertical(g1)
    c: Vertical(g3)
    c: Coincident(g4,g5)
    c: Coincident(g5,g6)
    c: Coincident(g6,g7)
    c: Coincident(g7,g4)
    c: Horizontal(g4)
    c: Horizontal(g6)
    c: Vertical(g5)
    c: Vertical(g7)
    c: Coincident(g8,g9)
    c: Coincident(g9,g10)
    c: Coincident(g10,g11)
    c: Coincident(g11,g8)
    c: Horizontal(g8)
    c: Horizontal(g10)
    c: Vertical(g9)
    c: Vertical(g11)
    c: Coincident(g12,g13)
    c: Coincident(g13,g14)
    c: Coincident(g14,g15)
    c: Coincident(g15,g12)
    c: Horizontal(g12)
    c: Horizontal(g14)
    c: Vertical(g13)
    c: Vertical(g15)
    c: Equal(g15,g9)
    c: Equal(g9,g1)
    c: Equal(g1,g7)
    c: Distance(g3) = 4
    c: Distance(g0) = 10
    c: Equal(g2,g6)
    c: Equal(g6,g8)
    c: Equal(g8,g12)
    c: Coincident(g16,g17)
    c: Coincident(g17,g18)
    c: Coincident(g18,g19)
    c: Coincident(g19,g16)
    c: Horizontal(g16)
    c: Horizontal(g18)
    c: Vertical(g17)
    c: Vertical(g19)
    c: Coincident(g1,g16)
    c: Coincident(g16,g6)
    c: Coincident(g12,g17)
    c: Coincident(g18,g8)
    c: Distance(g18) = 43
    c: Distance(g17) = 45
    c: DistanceX(g-1,g6) = -217.5
    c: DistanceY(g-1,g6) = -21
FEATURE [PartDesign::Pad] Pad013
  Length = 10
  Length2 = 100
  Placement = pos=(70,275,66) rot=(0.707107,0.707107,0;3.14159rad)
  Sketch = -> Sketch018
  Type = 0
FEATURE [Part::Cut] Cut113  label="chassis-src"
  Base = -> Fillet018013
  Placement = pos=(-275,70,2) rot=(0,0,-1;1.5708rad)
  Tool = -> Pad013
FEATURE [Part::FeaturePython] Clone025  label="Clone of chassis-src"  # Draft clone (typed FeaturePython)
  Objects = -> [Cut113]
  Placement = pos=(-275,70,2) rot=(0,0,-1;1.5708rad)
  Scale = (1,1,1)
FEATURE [Sketcher::SketchObject] Sketch019
  Placement = pos=(-119,23.5,141) rot=(0,0,1;1.5708rad)
  sketch-geometry (7):
    g0: Circle CenterX=37 CenterY=120 CenterZ=0 NormalX=0 NormalY=0 NormalZ=1 Radius=1.2
    g1: Circle CenterX=9.5 CenterY=120 CenterZ=0 NormalX=0 NormalY=0 NormalZ=1 Radius=1.2
    g2: LineSegment StartX=35.25 StartY=126.5 StartZ=0 EndX=11.25 EndY=126.5 EndZ=0
    g3: LineSegment StartX=11.25 StartY=126.5 StartZ=0 EndX=11.25 EndY=113.5 EndZ=0
    g4: LineSegment StartX=11.25 StartY=113.5 StartZ=0 EndX=35.25 EndY=113.5 EndZ=0
    g5: LineSegment StartX=35.25 StartY=113.5 StartZ=0 EndX=35.25 EndY=126.5 EndZ=0
    g6: LineSegment [constr] StartX=9.5 StartY=120 StartZ=0 EndX=37 EndY=120 EndZ=0
  constraints (20):
    c: Coincident(g2,g3)
    c: Coincident(g3,g4)
    c: Coincident(g4,g5)
    c: Coincident(g5,g2)
    c: Horizontal(g2)
    c: Horizontal(g4)
    c: Vertical(g3)
    c: Vertical(g5)
    c: Distance(g2) = 24
    c: Distance(g5) = 13
    c: Radius(g1) = 1.2
    c: Equal(g1,g0)
    c: Coincident(g0,g6)
    c: Coincident(g1,g6)
    c: Distance(g6) = 27.5
    c: Horizontal(g6)
    c: DistanceX(g-1,g1) = 9.5
    c: DistanceY(g1) = 120
    c: DistanceY(g1,g3) = -6.5
    c: DistanceX(g1,g2) = 1.75
FEATURE [PartDesign::Pad] Pad014
  Length = 16
  Length2 = 100
  Placement = pos=(-119,23.5,141) rot=(0,0,1;1.5708rad)
  Sketch = -> Sketch019
  Type = 0
FEATURE [Part::Box] Box067  label="Cubo013"
  Height = 15.5
  Length = 14
  Placement = pos=(-246,30,131) rot=(0,0,1;0rad)
  Width = 33.5
FEATURE [Part::Box] Box068  label="Cubo014"
  Height = 29.5
  Length = 14
  Placement = pos=(-246,34.75,132) rot=(0,0,1;0rad)
  Width = 24
FEATURE [Sketcher::SketchObject] Sketch020
  Placement = pos=(-232,0,0) rot=(0.57735,0.57735,0.57735;2.0944rad)
  sketch-geometry (12):
    g0: LineSegment StartX=58.7463 StartY=151.629 StartZ=0 EndX=56.7806 EndY=151.629 EndZ=0
    g1: LineSegment StartX=56.7806 StartY=151.629 StartZ=0 EndX=56.7806 EndY=160.733 EndZ=0
    g2: LineSegment StartX=56.7806 StartY=160.733 StartZ=0 EndX=58.7463 EndY=160.733 EndZ=0
    g3: LineSegment StartX=59.4575 StartY=151.357 StartZ=0 EndX=64.2177 EndY=147.084 EndZ=0
    g4: LineSegment StartX=70.0652 StartY=146.486 StartZ=0 EndX=68.6741 EndY=152.764 EndZ=0
    g5: ArcOfCircle CenterX=58.7463 CenterY=150.564 CenterZ=0 NormalX=0 NormalY=0 NormalZ=1 Radius=10.1685 StartAngle=0.218051 EndAngle=1.5708
    g6: ArcOfCircle CenterX=58.7463 CenterY=150.564 CenterZ=0 NormalX=0 NormalY=0 NormalZ=1 Radius=1.06462 StartAngle=0.839342 EndAngle=1.5708
    g7: LineSegment StartX=65.069 StartY=145.176 StartZ=0 EndX=65.069 EndY=134.871 EndZ=0
    g8: LineSegment StartX=65.069 StartY=134.871 StartZ=0 EndX=70.2829 EndY=134.871 EndZ=0
    g9: LineSegment StartX=70.2829 StartY=134.871 StartZ=0 EndX=70.2829 EndY=144.497 EndZ=0
    g10: ArcOfCircle CenterX=61.0884 CenterY=144.497 CenterZ=0 NormalX=0 NormalY=0 NormalZ=1 Radius=9.19448 StartAngle=0 EndAngle=0.218051
    g11: ArcOfCircle CenterX=62.5052 CenterY=145.176 CenterZ=0 NormalX=0 NormalY=0 NormalZ=1 Radius=2.56379 StartAngle=0 EndAngle=0.839342
  constraints (24):
    c: Horizontal(g0)
    c: Coincident(g0,g1)
    c: Vertical(g1)
    c: Coincident(g1,g2)
    c: Horizontal(g2)
    c: Coincident(g5,g2)
    c: Coincident(g5,g4)
    c: Coincident(g6,g0)
    c: Coincident(g6,g3)
    c: Tangent(g2,g5)
    c: Equal(g0,g6)
    c: Tangent(g5,g4)
    c: Coincident(g5,g6)
    c: Tangent(g6,g3)
    c: Tangent(g6,g0)
    c: Vertical(g7)
    c: Coincident(g7,g8)
    c: Horizontal(g8)
    c: Coincident(g8,g9)
    c: Vertical(g9)
    c: Tangent(g4,g10) = -1.5708
    c: Tangent(g9,g10) = -1.5708
    c: Tangent(g3,g11) = 1.5708
    c: Tangent(g7,g11) = 1.5708
FEATURE [PartDesign::Pad] Pad015
  Length = 14
  Length2 = 100
  Placement = pos=(-232,0,0) rot=(0.57735,0.57735,0.57735;2.0944rad)
  Reversed = true
  Sketch = -> Sketch020
  Type = 0
FEATURE [Part::MultiFuse] Fusion065  label="head-positive-cut"
  Shapes = -> [Box067,Pad015,Pad014,Box068]
FEATURE [Part::Box] Box069  label="Cubo015"
  Height = 7.5
  Length = 5
  Placement = pos=(9,97,127) rot=(0,0,1;0rad)
  Width = 12
FEATURE [Part::Cut] Cut114
  Base = -> Cut100
  Tool = -> Box069
FEATURE [App::DocumentObjectGroup] Grupo  label="src001"
  Group = -> [Cut091,Cut107,Fusion045,Cut113,Cut114]
FEATURE [App::DocumentObjectGroup] Group003  label="original-src"
  Group = -> [Part__Mirroring006,Part__Mirroring007,Group004,Group005,Grupo]
FEATURE [Part::Fillet] Fillet018013051
  Base = -> Cut114
  Edges = 1 edges r=0.5: [Edge83]
FEATURE [Part::FeaturePython] Clone026  label="Clone of arm"  # Draft clone (typed FeaturePython)
  Objects = -> [Fillet018013051]
  Placement = pos=(-275,70,2.5) rot=(0,0,-1;1.5708rad)
  Scale = (1,1,1)
FEATURE [Part::Mirroring] Part__Mirroring007016  label="Clone of arm001"
  Base = (0,0,0)
  Normal = (1,0,0)
  Placement = pos=(-478,0,0) rot=(0,0,1;0rad)
  Source = -> Clone026
FEATURE [Part::Prism] Prism  label="Prisma001"
  Circumradius = 3.3
  Height = 10
  Placement = pos=(18,85,84) rot=(-1,0,0;1.5708rad)
  Polygon = 6
FEATURE [Part::Prism] Prism002  label="Prisma002"
  Circumradius = 3.3
  Height = 10
  Placement = pos=(8,85,84) rot=(-1,0,0;1.5708rad)
  Polygon = 6
FEATURE [Part::Cylinder] Cylinder089  label="Cilindro017"
  Angle = 360
  Height = 32
  Placement = pos=(18,116,84) rot=(-1,0,0;1.5708rad)
  Radius = 3
FEATURE [Part::Cylinder] Cylinder090  label="Cilindro018"
  Angle = 360
  Height = 32
  Placement = pos=(8,116,84) rot=(-1,0,0;1.5708rad)
  Radius = 3
FEATURE [Part::Box] Box070  label="Cubo005"
  Height = 28
  Length = 20
  Placement = pos=(3.5,97.5,79.5) rot=(0,0,1;0rad)
  Width = 16
FEATURE [Part::Cylinder] Cylinder091  label="Cilindro013"
  Angle = 360
  Height = 32
  Placement = pos=(18,90,84) rot=(-1,0,0;1.5708rad)
  Radius = 1.75
FEATURE [Part::Cylinder] Cylinder092  label="Cilindro012"
  Angle = 360
  Height = 32
  Placement = pos=(8,90,84) rot=(-1,0,0;1.5708rad)
  Radius = 1.75
FEATURE [Part::MultiFuse] Fusion066  label="arm-positive-cut"
  Shapes = -> [Prism,Prism002,Cylinder089,Cylinder090,Box070,Cylinder091,Cylinder092]
FEATURE [Part::FeaturePython] Clone027  label="Clone of arm-positive-cut-left"  # Draft clone (typed FeaturePython)
  Objects = -> [Fusion066]
  Placement = pos=(-275,70,2.8) rot=(0,0,-1;1.5708rad)
  Scale = (1,1,1)
FEATURE [Part::Mirroring] Part__Mirroring007017  label="Clone of arm-positive-cut-right"
  Base = (0,0,0)
  Normal = (1,0,0)
  Placement = pos=(-478,0,0) rot=(0,0,1;0rad)
  Source = -> Clone027
FEATURE [Part::Feature] Part__Mirroring007013  label="pata-I001"
  Placement = pos=(-202.95,69.9,1.95) rot=(0,0,-1;1.5708rad)
  shape: bbox 21 x 53 x 59.5 mm, 32 faces (baked)
FEATURE [Part::Feature] Part__Mirroring007014  label="leg-body"
  Placement = pos=(-255.95,69.7,1.95) rot=(0,0,-1;1.5708rad)
  shape: bbox 21 x 53 x 59.5 mm, 32 faces (baked)
FEATURE [Part::FeaturePython] Clone028  label="Clone of left-shoulder"  # Draft clone (typed FeaturePython)
  Objects = -> [Part__Mirroring007012]
  Placement = pos=(-478,0,0) rot=(0,0,1;3.14159rad)
  Scale = (1,1,1)
FEATURE [Part::FeaturePython] Clone029  label="Clone of left-shoulder001"  # Draft clone (typed FeaturePython)
  Objects = -> [Part__Mirroring007012]
  Placement = pos=(-478,3,0) rot=(0,0,1;3.14159rad)
  Scale = (1,1,1)
FEATURE [Part::Box] Box071  label="Cube081"
  Height = 35
  Length = 47
  Placement = pos=(-205.102,65.2498,108.143) rot=(0,0,1;0rad)
  Width = 42
FEATURE [Part::Box] Box072  label="Cube082"
  Height = 35
  Length = 47
  Placement = pos=(-205.102,24.2498,108.143) rot=(0,0,1;0rad)
  Width = 42
FEATURE [Part::MultiCommon] Common
  Shapes = -> [Box071,Clone029]
FEATURE [Part::MultiCommon] Common001
  Shapes = -> [Box072,Clone028]
FEATURE [Part::MultiFuse] Fusion067  label="bigger_shoulder"
  Shapes = -> [Common001,Common]
FEATURE [Sketcher::SketchObject] Sketch021
  ExternalGeometry = -> [Cut109]
  Placement = pos=(0,0,133) rot=(0,0,1;0rad)
  Support = -> Cut109 [Face5]
  sketch-geometry (6):
    g0: Circle CenterX=-239 CenterY=59.25 CenterZ=0 NormalX=0 NormalY=0 NormalZ=1 Radius=1
    g1: Circle CenterX=-232.5 CenterY=52.75 CenterZ=0 NormalX=0 NormalY=0 NormalZ=1 Radius=1
    g2: Circle CenterX=-239 CenterY=46.25 CenterZ=0 NormalX=0 NormalY=0 NormalZ=1 Radius=1
    g3: Circle CenterX=-245.5 CenterY=52.75 CenterZ=0 NormalX=0 NormalY=0 NormalZ=1 Radius=1
    g4: LineSegment [constr] StartX=-239 StartY=59.25 StartZ=0 EndX=-239 EndY=46.25 EndZ=0
    g5: LineSegment [constr] StartX=-245.5 StartY=52.75 StartZ=0 EndX=-232.5 EndY=52.75 EndZ=0
  constraints (16):
    c: Radius(g3) = 1
    c: Equal(g3,g0)
    c: Equal(g3,g1)
    c: Equal(g3,g2)
    c: Coincident(g4,g0)
    c: Coincident(g4,g2)
    c: Coincident(g5,g3)
    c: Coincident(g5,g1)
    c: Horizontal(g5)
    c: Vertical(g4)
    c: Symmetric(g1,g3,g4)
    c: Symmetric(g0,g2,g5)
    c: Distance(g4) = 13
    c: Distance(g5) = 13
    c: DistanceX(g-3,g1) = 6.5
    c: DistanceY(g-3,g0) = 6.5
FEATURE [PartDesign::Pocket] Pocket017  label="body_more_holes"
  Length = 2
  Sketch = -> Sketch021
  Type = 0
FEATURE [Sketcher::SketchObject] Sketch022
  ExternalGeometry = -> [Fusion067]
  Placement = pos=(-186.118,0,0) rot=(0.57735,0.57735,0.57735;2.0944rad)
  Support = -> Fusion067 [Face9]
  sketch-geometry (6):
    g0: Circle CenterX=52.75 CenterY=129 CenterZ=0 NormalX=0 NormalY=0 NormalZ=1 Radius=1
    g1: Circle CenterX=59.25 CenterY=122.5 CenterZ=0 NormalX=0 NormalY=0 NormalZ=1 Radius=1
    g2: Circle CenterX=52.75 CenterY=116 CenterZ=0 NormalX=0 NormalY=0 NormalZ=1 Radius=1
    g3: Circle CenterX=46.25 CenterY=122.5 CenterZ=0 NormalX=0 NormalY=0 NormalZ=1 Radius=1
    g4: LineSegment [constr] StartX=52.75 StartY=129 StartZ=0 EndX=52.75 EndY=116 EndZ=0
    g5: LineSegment [constr] StartX=59.25 StartY=122.5 StartZ=0 EndX=46.25 EndY=122.5 EndZ=0
  constraints (16):
    c: Radius(g3) = 1
    c: Equal(g3,g0)
    c: Equal(g3,g1)
    c: Equal(g3,g2)
    c: Coincident(g4,g0)
    c: Coincident(g4,g2)
    c: Vertical(g4)
    c: Coincident(g5,g1)
    c: Coincident(g5,g3)
    c: Horizontal(g5)
    c: Symmetric(g1,g3,g4)
    c: Symmetric(g2,g0,g5)
    c: DistanceY(g4,g4) = 13
    c: DistanceX(g5,g5) = 13
    c: DistanceY(g-4,g0) = 6.5
    c: DistanceX(g3,g-4) = 6.5
FEATURE [PartDesign::Pocket] Pocket018
  Length = 3
  Sketch = -> Sketch022
  Type = 0
FEATURE [Sketcher::SketchObject] Sketch023
  ExternalGeometry = -> [Pocket018]
  Placement = pos=(0,29,0) rot=(1,0,0;1.5708rad)
  Support = -> Pocket018 [Face24]
  sketch-geometry (6):
    g0: Circle CenterX=-174.22 CenterY=133.896 CenterZ=0 NormalX=0 NormalY=0 NormalZ=1 Radius=1
    g1: Circle CenterX=-165.354 CenterY=131.47 CenterZ=0 NormalX=0 NormalY=0 NormalZ=1 Radius=1
    g2: Circle CenterX=-167.78 CenterY=122.604 CenterZ=0 NormalX=0 NormalY=0 NormalZ=1 Radius=1
    g3: Circle CenterX=-176.646 CenterY=125.03 CenterZ=0 NormalX=0 NormalY=0 NormalZ=1 Radius=1
    g4: LineSegment [constr] StartX=-176.646 StartY=125.03 StartZ=0 EndX=-165.354 EndY=131.47 EndZ=0
    g5: LineSegment [constr] StartX=-167.78 StartY=122.604 StartZ=0 EndX=-174.22 EndY=133.896 EndZ=0
  constraints (14):
    c: Coincident(g4,g1)
    c: Coincident(g5,g2)
    c: Coincident(g5,g0)
    c: Perpendicular(g4,g5)
    c: Distance(g4) = 13
    c: Distance(g5) = 13
    c: Symmetric(g1,g3,g5)
    c: Radius(g3) = 1
    c: Equal(g3,g0)
    c: Equal(g3,g1)
    c: Equal(g3,g2)
    c: Coincident(g3,g4)
    c: Symmetric(g4,g4,g-3)
    c: Symmetric(g5,g5,g-3)
FEATURE [PartDesign::Pocket] Pocket019  label="leftShoulder(large)_more_holes"
  Length = 4
  Sketch = -> Sketch023
  Type = 0
FEATURE [Sketcher::SketchObject] Sketch024
  ExternalGeometry = -> [Part__Mirroring007013]
  Placement = pos=(-202.95,28.1,1.95) rot=(1,0,0;1.5708rad)
  Support = -> Part__Mirroring007013 [Face6]
  sketch-geometry (9):
    g0: Circle CenterX=-16.85 CenterY=13 CenterZ=0 NormalX=0 NormalY=0 NormalZ=1 Radius=1
    g1: Circle CenterX=-15.8653 CenterY=16.675 CenterZ=0 NormalX=0 NormalY=0 NormalZ=1 Radius=1
    g2: Circle CenterX=-3.13471 CenterY=16.675 CenterZ=0 NormalX=0 NormalY=0 NormalZ=1 Radius=1
    g3: Circle CenterX=-2.15 CenterY=13 CenterZ=0 NormalX=0 NormalY=0 NormalZ=1 Radius=1
    g4: Circle CenterX=-9.5 CenterY=5.65 CenterZ=0 NormalX=0 NormalY=0 NormalZ=1 Radius=1
    g5: LineSegment [constr] StartX=-16.85 StartY=13 StartZ=0 EndX=-2.15 EndY=13 EndZ=0
    g6: LineSegment [constr] StartX=-9.5 StartY=20.35 StartZ=0 EndX=-9.5 EndY=5.65 EndZ=0
    g7: LineSegment [constr] StartX=-15.8653 StartY=16.675 StartZ=0 EndX=-9.5 EndY=13 EndZ=0
    g8: LineSegment [constr] StartX=-9.5 StartY=13 StartZ=0 EndX=-3.13471 EndY=16.675 EndZ=0
  constraints (23):
    c: Radius(g1) = 1
    c: Equal(g1,g2)
    c: Equal(g1,g3)
    c: Equal(g1,g4)
    c: Equal(g1,g0)
    c: Symmetric(g0,g3,g-3)
    c: Coincident(g5,g3)
    c: Horizontal(g5)
    c: Coincident(g0,g5)
    c: Coincident(g6,g-4)
    c: Vertical(g6)
    c: Symmetric(g6,g4,g-3)
    c: Coincident(g6,g4)
    c: DistanceX(g5,g5) = 14.7
    c: DistanceY(g6,g6) = 14.7
    c: Coincident(g7,g1)
    c: Coincident(g7,g-3)
    c: Coincident(g8,g7)
    c: Coincident(g8,g2)
    c: Angle(g5,g8) = 0.523599
    c: Angle(g7,g5) = 0.523599
    c: Distance(g7) = 7.35
    c: Distance(g8) = 7.35
FEATURE [PartDesign::Pocket] Pocket020
  Length = 3
  Placement = pos=(-202.95,69.9,1.95) rot=(0,0,-1;1.5708rad)
  Sketch = -> Sketch024
  Type = 0
FEATURE [Sketcher::SketchObject] Sketch025
  ExternalGeometry = -> [Pocket020]
  Placement = pos=(-202.95,69.9,63.95) rot=(0,0,-1;1.5708rad)
  Support = -> Pocket020 [Face5]
  sketch-geometry (9):
    g0: Circle CenterX=9.65 CenterY=-9.5 CenterZ=0 NormalX=0 NormalY=0 NormalZ=1 Radius=1
    g1: Circle CenterX=17 CenterY=-2.15 CenterZ=0 NormalX=0 NormalY=0 NormalZ=1 Radius=1
    g2: Circle CenterX=20.675 CenterY=-3.13471 CenterZ=0 NormalX=0 NormalY=0 NormalZ=1 Radius=1
    g3: Circle CenterX=20.675 CenterY=-15.8653 CenterZ=0 NormalX=0 NormalY=0 NormalZ=1 Radius=1
    g4: Circle CenterX=17 CenterY=-16.85 CenterZ=0 NormalX=0 NormalY=0 NormalZ=1 Radius=1
    g5: LineSegment [constr] StartX=17 StartY=-2.15 StartZ=0 EndX=17 EndY=-16.85 EndZ=0
    g6: LineSegment [constr] StartX=9.65 StartY=-9.5 StartZ=0 EndX=24.35 EndY=-9.5 EndZ=0
    g7: LineSegment [constr] StartX=20.675 StartY=-15.8653 StartZ=0 EndX=17 EndY=-9.5 EndZ=0
    g8: LineSegment [constr] StartX=17 StartY=-9.5 StartZ=0 EndX=20.675 EndY=-3.13471 EndZ=0
  constraints (22):
    c: Radius(g1) = 1
    c: Equal(g1,g2)
    c: Equal(g1,g3)
    c: Equal(g1,g4)
    c: Equal(g1,g0)
    c: Symmetric(g1,g4,g-3)
    c: Coincident(g5,g1)
    c: Coincident(g5,g4)
    c: Vertical(g5)
    c: Coincident(g6,g-4)
    c: Horizontal(g6)
    c: Coincident(g0,g6)
    c: Symmetric(g0,g6,g-3)
    c: DistanceY(g5,g5) = 14.7
    c: Coincident(g7,g3)
    c: Coincident(g7,g-3)
    c: Coincident(g8,g7)
    c: Coincident(g8,g2)
    c: Angle(g8,g5) = 0.523599
    c: Angle(g5,g7) = 0.523599
    c: Distance(g8) = 7.35
    c: Distance(g7) = 7.35
FEATURE [PartDesign::Pocket] Pocket021  label="LeftLeg_more_holes"
  Length = 3
  Placement = pos=(-202.95,69.9,1.95) rot=(0,0,-1;1.5708rad)
  Sketch = -> Sketch025
  Type = 0
FEATURE [App::DocumentObjectGroup] Group017  label="Assembly"
  Group = -> [Fusion043,Part__Mirroring007012,Part__Mirroring007016,Part__Mirroring007014,Part__Mirroring007013,Part__Mirroring007015,Cut112,Clone025,Pocket020,Pocket021]
FEATURE [Part::Box] Box073  label="Cubo016"
  Height = 50
  Length = 50
  Placement = pos=(-266.203,25.3421,131) rot=(0,0,1;0rad)
  Width = 50
FEATURE [Mesh::Feature] Robot_Head
FEATURE [Part::Feature] Robot_Head001
  shape: bbox 100 x 100 x 64.01 mm, 4570 faces, 0 solids (baked)
FEATURE [Part::Feature] Robot_Head001001  label="Robot_Head002"
  shape: bbox 100 x 100 x 64.01 mm, 3905 faces, 0 solids (baked)
FEATURE [Part::Feature] Robot_Head001001_solid  label="Robot_Head002 (Solid)"
  shape: bbox 100 x 100 x 64.01 mm, 3905 faces (baked)
FEATURE [Part::Box] Box074  label="Cubo017"
  Height = 50
  Length = 50
  Placement = pos=(-21.2,-21.8852,127.8) rot=(0,0,1;0rad)
  Width = 50
FEATURE [Part::Cut] Cut115
  Base = -> Robot_Head001001_solid
  Placement = pos=(-238.9,43.25,-46.7) rot=(0,0,1;0rad)
  Tool = -> Box074
FEATURE [Part::FeaturePython] Clone030  label="Clone of Cut115"  # Draft clone (typed FeaturePython)
  Objects = -> [Cut115]
  Placement = pos=(-298.75,54.9,-8) rot=(0,0,1;0rad)
  Scale = (0.75,0.75,0.75)
FEATURE [Part::Feature] Cut116001  label="makerbot_head001"
  shape: bbox 75 x 75.02 x 40.56 mm, 3878 faces (baked)
FEATURE [Part::Cut] Cut116002  label="maker_bot_head"
  Base = -> Clone030
  Tool = -> Fusion065
FEATURE [Part::Feature] Cut116002001  label="maker_bot_head001"
  shape: bbox 75 x 75.02 x 40.56 mm, 3877 faces (baked)
